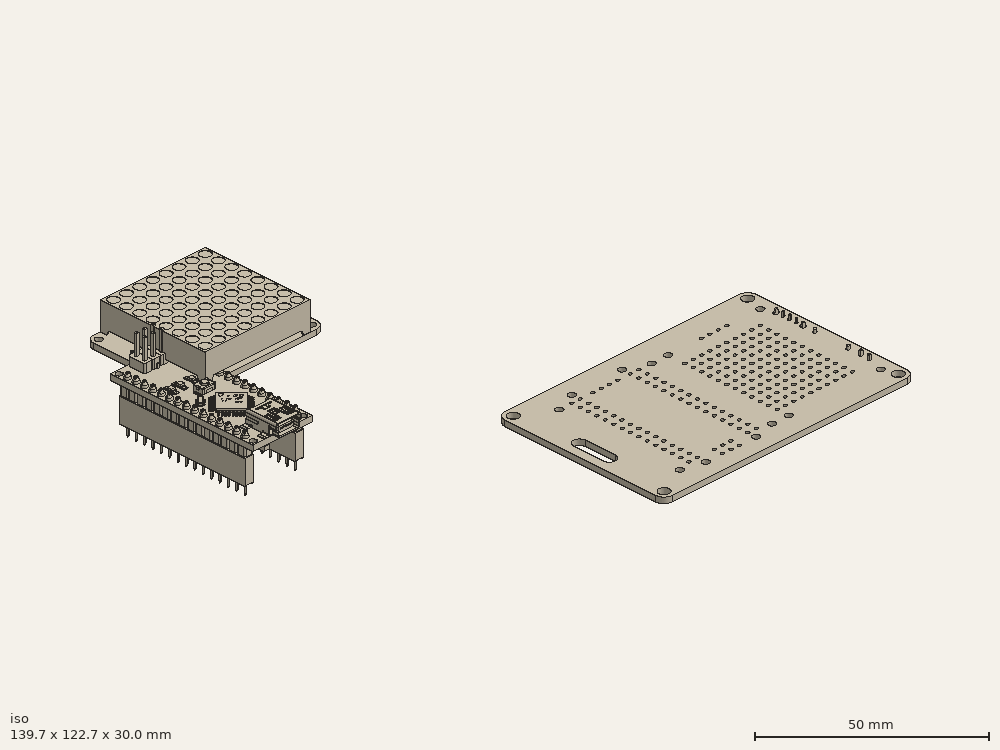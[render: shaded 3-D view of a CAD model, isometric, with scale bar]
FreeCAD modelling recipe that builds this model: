
FCSTD DOCUMENT  (FreeCAD 2022.709R28846 (Git))
Label: 8x8_badge
License: All rights reserved
LicenseURL: http://en.wikipedia.org/wiki/All_rights_reserved
objects: App::Link×150, Part::Feature×100, App::Part×8, PartDesign::CoordinateSystem×1, Sketcher::SketchObject×1
note: 102 computed .brp shape members not serialized (recipe doc carries the construction recipe); baked Part::Feature solids carry a one-line shape summary decoded from their .brp

FEATURE [PartDesign::CoordinateSystem] Local_CS_97b0
  AttacherType = Attacher::AttachEngine3D
  AttachmentSupport = -> [X_Axis001]
  MapMode = 2
  Support = -> [X_Axis001]
  TreeRank = 0
FEATURE [Part::Feature] Pcb_97b0
  TreeRank = 0
  shape: bbox 76.2 x 50.8 x 1.6 mm, 233 faces (baked)
FEATURE [Sketcher::SketchObject] PCB_Sketch_97b0
  ArcFitTolerance = 0
  FullyConstrained = false
  TreeRank = 0
  sketch-geometry (16):
    g0: LineSegment StartX=56.896 StartY=-85.852 StartZ=0 EndX=56.896 EndY=-76.708 EndZ=0
    g1: LineSegment StartX=53.34 StartY=-55.88 StartZ=0 EndX=124.46 EndY=-55.88 EndZ=0
    g2: LineSegment StartX=124.46 StartY=-106.68 StartZ=0 EndX=53.34 EndY=-106.68 EndZ=0
    g3: LineSegment StartX=127 StartY=-58.42 StartZ=0 EndX=127 EndY=-104.14 EndZ=0
    g4: LineSegment StartX=53.34 StartY=-76.708 StartZ=0 EndX=53.34 EndY=-85.852 EndZ=0
    g5: LineSegment StartX=50.8 StartY=-104.14 StartZ=0 EndX=50.8 EndY=-58.42 EndZ=0
    g6: ArcOfCircle CenterX=124.46 CenterY=-58.42 CenterZ=0 NormalX=0 NormalY=0 NormalZ=-1 AngleXU=1.5708 Radius=2.54 StartAngle=0 EndAngle=1.5708
    g7: ArcOfCircle CenterX=53.34 CenterY=-58.42 CenterZ=0 NormalX=0 NormalY=0 NormalZ=-1 AngleXU=3.01383e-07 Radius=2.54 StartAngle=0 EndAngle=1.5708
    g8: ArcOfCircle CenterX=55.118 CenterY=-85.852 CenterZ=0 NormalX=0 NormalY=0 NormalZ=-1 AngleXU=-3.14159 Radius=1.778 StartAngle=0 EndAngle=3.14159
    g9: ArcOfCircle CenterX=55.118 CenterY=-76.708 CenterZ=0 NormalX=0 NormalY=0 NormalZ=-1 AngleXU=8e-15 Radius=1.778 StartAngle=0 EndAngle=3.14159
    g10: ArcOfCircle CenterX=53.34 CenterY=-104.14 CenterZ=0 NormalX=0 NormalY=0 NormalZ=-1 AngleXU=-1.5708 Radius=2.54 StartAngle=0 EndAngle=1.5708
    g11: ArcOfCircle CenterX=124.46 CenterY=-104.14 CenterZ=0 NormalX=0 NormalY=0 NormalZ=-1 AngleXU=-3.14159 Radius=2.54 StartAngle=0 EndAngle=1.5708
    g12: Circle CenterX=124.46 CenterY=-58.42 CenterZ=0 NormalX=0 NormalY=0 NormalZ=1 AngleXU=0 Radius=1.524
    g13: Circle CenterX=53.34 CenterY=-104.14 CenterZ=0 NormalX=0 NormalY=0 NormalZ=1 AngleXU=0 Radius=1.524
    g14: Circle CenterX=124.46 CenterY=-104.14 CenterZ=0 NormalX=0 NormalY=0 NormalZ=1 AngleXU=0 Radius=1.524
    g15: Circle CenterX=53.34 CenterY=-58.42 CenterZ=0 NormalX=0 NormalY=0 NormalZ=1 AngleXU=0 Radius=1.524
  constraints (12):
    c: Coincident(g5,g10)
    c: Coincident(g5,g7)
    c: Coincident(g2,g10)
    c: Coincident(g4,g8)
    c: Coincident(g4,g9)
    c: Coincident(g1,g7)
    c: Coincident(g0,g8)
    c: Coincident(g0,g9)
    c: Coincident(g2,g11)
    c: Coincident(g1,g6)
    c: Coincident(g3,g11)
    c: Coincident(g3,g6)
FEATURE [Part::Feature] Shape  label="J135_PinHeader_1x01_P254mm_Vertical_da6c4aed0287"
  Placement = pos=(102.87,-71.12,0) rot=(0,0,1;1.5708rad)
  TreeRank = 0
  shape: bbox 2.54 x 2.54 x 11.54 mm, 28 faces (baked)
FEATURE [App::Link] J135_PinHeader_1x01_P254mm_Vertical_da6c4aed0287_ln_  label="J61_PinHeader_1x01_P254mm_Vertical_773ae547e81d"
  AutoLinkLabel = false
  AutoPlacement = true
  LinkPlacement = pos=(118.11,-91.44,0) rot=(0,0,1;1.5708rad)
  LinkedObject = -> Shape
  Placement = pos=(118.11,-91.44,0) rot=(0,0,1;1.5708rad)
  SyncGroupVisibility = false
  TreeRank = 0
  _LinkVersion = 1
FEATURE [App::Link] J135_PinHeader_1x01_P254mm_Vertical_da6c4aed0287_ln_001  label="J50_PinHeader_1x01_P254mm_Vertical_5aa259a9185c"
  AutoLinkLabel = false
  AutoPlacement = true
  LinkPlacement = pos=(115.57,-93.98,0) rot=(0,0,1;1.5708rad)
  LinkedObject = -> Shape
  Placement = pos=(115.57,-93.98,0) rot=(0,0,1;1.5708rad)
  SyncGroupVisibility = false
  TreeRank = 0
  _LinkVersion = 1
FEATURE [App::Link] J135_PinHeader_1x01_P254mm_Vertical_da6c4aed0287_ln_002  label="J2_PinHeader_1x01_P254mm_Vertical_c9b2285a6f13"
  AutoLinkLabel = false
  AutoPlacement = true
  LinkPlacement = pos=(66.04,-88.9,0) rot=(0,0,1;3.14159rad)
  LinkedObject = -> Shape
  Placement = pos=(66.04,-88.9,0) rot=(0,0,1;3.14159rad)
  SyncGroupVisibility = false
  TreeRank = 0
  _LinkVersion = 1
FEATURE [App::Link] J135_PinHeader_1x01_P254mm_Vertical_da6c4aed0287_ln_003  label="J140_PinHeader_1x01_P254mm_Vertical_72f53bb47756"
  AutoLinkLabel = false
  AutoPlacement = true
  LinkPlacement = pos=(115.57,-71.12,0) rot=(0,0,1;1.5708rad)
  LinkedObject = -> Shape
  Placement = pos=(115.57,-71.12,0) rot=(0,0,1;1.5708rad)
  SyncGroupVisibility = false
  TreeRank = 0
  _LinkVersion = 1
FEATURE [App::Link] J135_PinHeader_1x01_P254mm_Vertical_da6c4aed0287_ln_004  label="J124_PinHeader_1x01_P254mm_Vertical_2792789bb18d"
  AutoLinkLabel = false
  AutoPlacement = true
  LinkPlacement = pos=(100.33,-73.66,0) rot=(0,0,1;1.5708rad)
  LinkedObject = -> Shape
  Placement = pos=(100.33,-73.66,0) rot=(0,0,1;1.5708rad)
  SyncGroupVisibility = false
  TreeRank = 0
  _LinkVersion = 1
FEATURE [App::Link] J135_PinHeader_1x01_P254mm_Vertical_da6c4aed0287_ln_005  label="J17_PinHeader_1x01_P254mm_Vertical_b3db6972f96f"
  AutoLinkLabel = false
  AutoPlacement = true
  LinkPlacement = pos=(66.04,-99.06,0) rot=(0,0,1;3.14159rad)
  LinkedObject = -> Shape
  Placement = pos=(66.04,-99.06,0) rot=(0,0,1;3.14159rad)
  SyncGroupVisibility = false
  TreeRank = 0
  _LinkVersion = 1
FEATURE [App::Link] J135_PinHeader_1x01_P254mm_Vertical_da6c4aed0287_ln_006  label="J44_PinHeader_1x01_P254mm_Vertical_6a244c9ca252"
  AutoLinkLabel = false
  AutoPlacement = true
  LinkPlacement = pos=(100.33,-93.98,0) rot=(0,0,1;1.5708rad)
  LinkedObject = -> Shape
  Placement = pos=(100.33,-93.98,0) rot=(0,0,1;1.5708rad)
  SyncGroupVisibility = false
  TreeRank = 0
  _LinkVersion = 1
FEATURE [App::Link] J135_PinHeader_1x01_P254mm_Vertical_da6c4aed0287_ln_007  label="J69_PinHeader_1x01_P254mm_Vertical_9c543508d3f7"
  AutoLinkLabel = false
  AutoPlacement = true
  LinkPlacement = pos=(113.03,-88.9,0) rot=(0,0,1;1.5708rad)
  LinkedObject = -> Shape
  Placement = pos=(113.03,-88.9,0) rot=(0,0,1;1.5708rad)
  SyncGroupVisibility = false
  TreeRank = 0
  _LinkVersion = 1
FEATURE [App::Link] J135_PinHeader_1x01_P254mm_Vertical_da6c4aed0287_ln_008  label="J73_PinHeader_1x01_P254mm_Vertical_27754063a736"
  AutoLinkLabel = false
  AutoPlacement = true
  LinkPlacement = pos=(97.79,-86.36,0) rot=(0,0,1;1.5708rad)
  LinkedObject = -> Shape
  Placement = pos=(97.79,-86.36,0) rot=(0,0,1;1.5708rad)
  SyncGroupVisibility = false
  TreeRank = 0
  _LinkVersion = 1
FEATURE [App::Link] J135_PinHeader_1x01_P254mm_Vertical_da6c4aed0287_ln_009  label="J10_PinHeader_1x01_P254mm_Vertical_bf699268af4c"
  AutoLinkLabel = false
  AutoPlacement = true
  LinkPlacement = pos=(66.04,-68.58,0) rot=(0,0,1;3.14159rad)
  LinkedObject = -> Shape
  Placement = pos=(66.04,-68.58,0) rot=(0,0,1;3.14159rad)
  SyncGroupVisibility = false
  TreeRank = 0
  _LinkVersion = 1
FEATURE [App::Link] J135_PinHeader_1x01_P254mm_Vertical_da6c4aed0287_ln_010  label="J59_PinHeader_1x01_P254mm_Vertical_64cb25116942"
  AutoLinkLabel = false
  AutoPlacement = true
  LinkPlacement = pos=(113.03,-91.44,0) rot=(0,0,1;1.5708rad)
  LinkedObject = -> Shape
  Placement = pos=(113.03,-91.44,0) rot=(0,0,1;1.5708rad)
  SyncGroupVisibility = false
  TreeRank = 0
  _LinkVersion = 1
FEATURE [App::Link] J135_PinHeader_1x01_P254mm_Vertical_da6c4aed0287_ln_011  label="J41_PinHeader_1x01_P254mm_Vertical_46e97698a8e3"
  AutoLinkLabel = false
  AutoPlacement = true
  LinkPlacement = pos=(118.11,-96.52,0) rot=(0,0,1;1.5708rad)
  LinkedObject = -> Shape
  Placement = pos=(118.11,-96.52,0) rot=(0,0,1;1.5708rad)
  SyncGroupVisibility = false
  TreeRank = 0
  _LinkVersion = 1
FEATURE [App::Link] J135_PinHeader_1x01_P254mm_Vertical_da6c4aed0287_ln_012  label="J68_PinHeader_1x01_P254mm_Vertical_3277878d9fcc"
  AutoLinkLabel = false
  AutoPlacement = true
  LinkPlacement = pos=(110.49,-88.9,0) rot=(0,0,1;1.5708rad)
  LinkedObject = -> Shape
  Placement = pos=(110.49,-88.9,0) rot=(0,0,1;1.5708rad)
  SyncGroupVisibility = false
  TreeRank = 0
  _LinkVersion = 1
FEATURE [App::Link] J135_PinHeader_1x01_P254mm_Vertical_da6c4aed0287_ln_013  label="J106_PinHeader_1x01_P254mm_Vertical_6a619a310b17"
  AutoLinkLabel = false
  AutoPlacement = true
  LinkPlacement = pos=(105.41,-78.74,0) rot=(0,0,1;1.5708rad)
  LinkedObject = -> Shape
  Placement = pos=(105.41,-78.74,0) rot=(0,0,1;1.5708rad)
  SyncGroupVisibility = false
  TreeRank = 0
  _LinkVersion = 1
FEATURE [App::Link] J135_PinHeader_1x01_P254mm_Vertical_da6c4aed0287_ln_014  label="J27_PinHeader_1x01_P254mm_Vertical_58b75af8ef85"
  AutoLinkLabel = false
  AutoPlacement = true
  LinkPlacement = pos=(86.36,-99.06,0) rot=(0,0,1;3.14159rad)
  LinkedObject = -> Shape
  Placement = pos=(86.36,-99.06,0) rot=(0,0,1;3.14159rad)
  SyncGroupVisibility = false
  TreeRank = 0
  _LinkVersion = 1
FEATURE [App::Link] J135_PinHeader_1x01_P254mm_Vertical_da6c4aed0287_ln_015  label="J95_PinHeader_1x01_P254mm_Vertical_eca1b71ce0e1"
  AutoLinkLabel = false
  AutoPlacement = true
  LinkPlacement = pos=(102.87,-81.28,0) rot=(0,0,1;1.5708rad)
  LinkedObject = -> Shape
  Placement = pos=(102.87,-81.28,0) rot=(0,0,1;1.5708rad)
  SyncGroupVisibility = false
  TreeRank = 0
  _LinkVersion = 1
FEATURE [App::Link] J135_PinHeader_1x01_P254mm_Vertical_da6c4aed0287_ln_016  label="J24_PinHeader_1x01_P254mm_Vertical_b4f680f1af2d"
  AutoLinkLabel = false
  AutoPlacement = true
  LinkPlacement = pos=(86.36,-73.66,0) rot=(0,0,1;3.14159rad)
  LinkedObject = -> Shape
  Placement = pos=(86.36,-73.66,0) rot=(0,0,1;3.14159rad)
  SyncGroupVisibility = false
  TreeRank = 0
  _LinkVersion = 1
FEATURE [App::Link] J135_PinHeader_1x01_P254mm_Vertical_da6c4aed0287_ln_017  label="J16_PinHeader_1x01_P254mm_Vertical_e98a18c1f6ef"
  AutoLinkLabel = false
  AutoPlacement = true
  LinkPlacement = pos=(66.04,-96.52,0) rot=(0,0,1;3.14159rad)
  LinkedObject = -> Shape
  Placement = pos=(66.04,-96.52,0) rot=(0,0,1;3.14159rad)
  SyncGroupVisibility = false
  TreeRank = 0
  _LinkVersion = 1
FEATURE [App::Link] J135_PinHeader_1x01_P254mm_Vertical_da6c4aed0287_ln_018  label="J77_PinHeader_1x01_P254mm_Vertical_00ab3d87ffcd"
  AutoLinkLabel = false
  AutoPlacement = true
  LinkPlacement = pos=(107.95,-86.36,0) rot=(0,0,1;1.5708rad)
  LinkedObject = -> Shape
  Placement = pos=(107.95,-86.36,0) rot=(0,0,1;1.5708rad)
  SyncGroupVisibility = false
  TreeRank = 0
  _LinkVersion = 1
FEATURE [App::Link] J135_PinHeader_1x01_P254mm_Vertical_da6c4aed0287_ln_019  label="J109_PinHeader_1x01_P254mm_Vertical_e80f5348a3fd"
  AutoLinkLabel = false
  AutoPlacement = true
  LinkPlacement = pos=(113.03,-78.74,0) rot=(0,0,1;1.5708rad)
  LinkedObject = -> Shape
  Placement = pos=(113.03,-78.74,0) rot=(0,0,1;1.5708rad)
  SyncGroupVisibility = false
  TreeRank = 0
  _LinkVersion = 1
FEATURE [App::Link] J135_PinHeader_1x01_P254mm_Vertical_da6c4aed0287_ln_020  label="J139_PinHeader_1x01_P254mm_Vertical_62e98df2bb86"
  AutoLinkLabel = false
  AutoPlacement = true
  LinkPlacement = pos=(113.03,-71.12,0) rot=(0,0,1;1.5708rad)
  LinkedObject = -> Shape
  Placement = pos=(113.03,-71.12,0) rot=(0,0,1;1.5708rad)
  SyncGroupVisibility = false
  TreeRank = 0
  _LinkVersion = 1
FEATURE [App::Link] J135_PinHeader_1x01_P254mm_Vertical_da6c4aed0287_ln_021  label="J123_PinHeader_1x01_P254mm_Vertical_de5b5ec60197"
  AutoLinkLabel = false
  AutoPlacement = true
  LinkPlacement = pos=(97.79,-73.66,0) rot=(0,0,1;1.5708rad)
  LinkedObject = -> Shape
  Placement = pos=(97.79,-73.66,0) rot=(0,0,1;1.5708rad)
  SyncGroupVisibility = false
  TreeRank = 0
  _LinkVersion = 1
FEATURE [App::Link] J135_PinHeader_1x01_P254mm_Vertical_da6c4aed0287_ln_022  label="J5_PinHeader_1x01_P254mm_Vertical_cd3758c55ec9"
  AutoLinkLabel = false
  AutoPlacement = true
  LinkPlacement = pos=(66.04,-81.28,0) rot=(0,0,1;3.14159rad)
  LinkedObject = -> Shape
  Placement = pos=(66.04,-81.28,0) rot=(0,0,1;3.14159rad)
  SyncGroupVisibility = false
  TreeRank = 0
  _LinkVersion = 1
FEATURE [App::Link] J135_PinHeader_1x01_P254mm_Vertical_da6c4aed0287_ln_023  label="J98_PinHeader_1x01_P254mm_Vertical_84919f920f7b"
  AutoLinkLabel = false
  AutoPlacement = true
  LinkPlacement = pos=(110.49,-81.28,0) rot=(0,0,1;1.5708rad)
  LinkedObject = -> Shape
  Placement = pos=(110.49,-81.28,0) rot=(0,0,1;1.5708rad)
  SyncGroupVisibility = false
  TreeRank = 0
  _LinkVersion = 1
FEATURE [App::Link] J135_PinHeader_1x01_P254mm_Vertical_da6c4aed0287_ln_024  label="J85_PinHeader_1x01_P254mm_Vertical_de25c8d6ebfc"
  AutoLinkLabel = false
  AutoPlacement = true
  LinkPlacement = pos=(102.87,-83.82,0) rot=(0,0,1;1.5708rad)
  LinkedObject = -> Shape
  Placement = pos=(102.87,-83.82,0) rot=(0,0,1;1.5708rad)
  SyncGroupVisibility = false
  TreeRank = 0
  _LinkVersion = 1
FEATURE [App::Link] J135_PinHeader_1x01_P254mm_Vertical_da6c4aed0287_ln_025  label="J78_PinHeader_1x01_P254mm_Vertical_6cd363f12a80"
  AutoLinkLabel = false
  AutoPlacement = true
  LinkPlacement = pos=(110.49,-86.36,0) rot=(0,0,1;1.5708rad)
  LinkedObject = -> Shape
  Placement = pos=(110.49,-86.36,0) rot=(0,0,1;1.5708rad)
  SyncGroupVisibility = false
  TreeRank = 0
  _LinkVersion = 1
FEATURE [App::Link] J135_PinHeader_1x01_P254mm_Vertical_da6c4aed0287_ln_026  label="J92_PinHeader_1x01_P254mm_Vertical_7b98299fb2b6"
  AutoLinkLabel = false
  AutoPlacement = true
  LinkPlacement = pos=(95.25,-81.28,0) rot=(0,0,1;1.5708rad)
  LinkedObject = -> Shape
  Placement = pos=(95.25,-81.28,0) rot=(0,0,1;1.5708rad)
  SyncGroupVisibility = false
  TreeRank = 0
  _LinkVersion = 1
FEATURE [App::Link] J135_PinHeader_1x01_P254mm_Vertical_da6c4aed0287_ln_027  label="J146_PinHeader_1x01_P254mm_Vertical_d33f2c13bd96"
  AutoLinkLabel = false
  AutoPlacement = true
  LinkPlacement = pos=(105.41,-68.58,0) rot=(0,0,1;1.5708rad)
  LinkedObject = -> Shape
  Placement = pos=(105.41,-68.58,0) rot=(0,0,1;1.5708rad)
  SyncGroupVisibility = false
  TreeRank = 0
  _LinkVersion = 1
FEATURE [App::Link] J135_PinHeader_1x01_P254mm_Vertical_da6c4aed0287_ln_028  label="J12_PinHeader_1x01_P254mm_Vertical_9e959caa93af"
  AutoLinkLabel = false
  AutoPlacement = true
  LinkPlacement = pos=(66.04,-63.5,0) rot=(0,0,1;3.14159rad)
  LinkedObject = -> Shape
  Placement = pos=(66.04,-63.5,0) rot=(0,0,1;3.14159rad)
  SyncGroupVisibility = false
  TreeRank = 0
  _LinkVersion = 1
FEATURE [App::Link] J135_PinHeader_1x01_P254mm_Vertical_da6c4aed0287_ln_029  label="J74_PinHeader_1x01_P254mm_Vertical_ebb3536fd29e"
  AutoLinkLabel = false
  AutoPlacement = true
  LinkPlacement = pos=(100.33,-86.36,0) rot=(0,0,1;1.5708rad)
  LinkedObject = -> Shape
  Placement = pos=(100.33,-86.36,0) rot=(0,0,1;1.5708rad)
  SyncGroupVisibility = false
  TreeRank = 0
  _LinkVersion = 1
FEATURE [App::Link] J135_PinHeader_1x01_P254mm_Vertical_da6c4aed0287_ln_030  label="J58_PinHeader_1x01_P254mm_Vertical_9a14729430aa"
  AutoLinkLabel = false
  AutoPlacement = true
  LinkPlacement = pos=(110.49,-91.44,0) rot=(0,0,1;1.5708rad)
  LinkedObject = -> Shape
  Placement = pos=(110.49,-91.44,0) rot=(0,0,1;1.5708rad)
  SyncGroupVisibility = false
  TreeRank = 0
  _LinkVersion = 1
FEATURE [App::Link] J135_PinHeader_1x01_P254mm_Vertical_da6c4aed0287_ln_031  label="J130_PinHeader_1x01_P254mm_Vertical_e60d4ac48af7"
  AutoLinkLabel = false
  AutoPlacement = true
  LinkPlacement = pos=(115.57,-73.66,0) rot=(0,0,1;1.5708rad)
  LinkedObject = -> Shape
  Placement = pos=(115.57,-73.66,0) rot=(0,0,1;1.5708rad)
  SyncGroupVisibility = false
  TreeRank = 0
  _LinkVersion = 1
FEATURE [App::Link] J135_PinHeader_1x01_P254mm_Vertical_da6c4aed0287_ln_032  label="J99_PinHeader_1x01_P254mm_Vertical_5f2264147a32"
  AutoLinkLabel = false
  AutoPlacement = true
  LinkPlacement = pos=(113.03,-81.28,0) rot=(0,0,1;1.5708rad)
  LinkedObject = -> Shape
  Placement = pos=(113.03,-81.28,0) rot=(0,0,1;1.5708rad)
  SyncGroupVisibility = false
  TreeRank = 0
  _LinkVersion = 1
FEATURE [App::Link] J135_PinHeader_1x01_P254mm_Vertical_da6c4aed0287_ln_033  label="J107_PinHeader_1x01_P254mm_Vertical_2f2c6f5fa7e0"
  AutoLinkLabel = false
  AutoPlacement = true
  LinkPlacement = pos=(107.95,-78.74,0) rot=(0,0,1;1.5708rad)
  LinkedObject = -> Shape
  Placement = pos=(107.95,-78.74,0) rot=(0,0,1;1.5708rad)
  SyncGroupVisibility = false
  TreeRank = 0
  _LinkVersion = 1
FEATURE [App::Link] J135_PinHeader_1x01_P254mm_Vertical_da6c4aed0287_ln_034  label="J117_PinHeader_1x01_P254mm_Vertical_64dd41409d9f"
  AutoLinkLabel = false
  AutoPlacement = true
  LinkPlacement = pos=(107.95,-76.2,0) rot=(0,0,1;1.5708rad)
  LinkedObject = -> Shape
  Placement = pos=(107.95,-76.2,0) rot=(0,0,1;1.5708rad)
  SyncGroupVisibility = false
  TreeRank = 0
  _LinkVersion = 1
FEATURE [App::Link] J135_PinHeader_1x01_P254mm_Vertical_da6c4aed0287_ln_035  label="J60_PinHeader_1x01_P254mm_Vertical_14a406c96dca"
  AutoLinkLabel = false
  AutoPlacement = true
  LinkPlacement = pos=(115.57,-91.44,0) rot=(0,0,1;1.5708rad)
  LinkedObject = -> Shape
  Placement = pos=(115.57,-91.44,0) rot=(0,0,1;1.5708rad)
  SyncGroupVisibility = false
  TreeRank = 0
  _LinkVersion = 1
FEATURE [App::Link] J135_PinHeader_1x01_P254mm_Vertical_da6c4aed0287_ln_036  label="J144_PinHeader_1x01_P254mm_Vertical_684e6d7036d3"
  AutoLinkLabel = false
  AutoPlacement = true
  LinkPlacement = pos=(100.33,-68.58,0) rot=(0,0,1;1.5708rad)
  LinkedObject = -> Shape
  Placement = pos=(100.33,-68.58,0) rot=(0,0,1;1.5708rad)
  SyncGroupVisibility = false
  TreeRank = 0
  _LinkVersion = 1
FEATURE [App::Link] J135_PinHeader_1x01_P254mm_Vertical_da6c4aed0287_ln_037  label="J3_PinHeader_1x01_P254mm_Vertical_85c80b18d1db"
  AutoLinkLabel = false
  AutoPlacement = true
  LinkPlacement = pos=(66.04,-86.36,0) rot=(0,0,1;3.14159rad)
  LinkedObject = -> Shape
  Placement = pos=(66.04,-86.36,0) rot=(0,0,1;3.14159rad)
  SyncGroupVisibility = false
  TreeRank = 0
  _LinkVersion = 1
FEATURE [App::Link] J135_PinHeader_1x01_P254mm_Vertical_da6c4aed0287_ln_038  label="J113_PinHeader_1x01_P254mm_Vertical_3395830e7b0b"
  AutoLinkLabel = false
  AutoPlacement = true
  LinkPlacement = pos=(97.79,-76.2,0) rot=(0,0,1;1.5708rad)
  LinkedObject = -> Shape
  Placement = pos=(97.79,-76.2,0) rot=(0,0,1;1.5708rad)
  SyncGroupVisibility = false
  TreeRank = 0
  _LinkVersion = 1
FEATURE [App::Link] J135_PinHeader_1x01_P254mm_Vertical_da6c4aed0287_ln_039  label="J90_PinHeader_1x01_P254mm_Vertical_ad3d40650960"
  AutoLinkLabel = false
  AutoPlacement = true
  LinkPlacement = pos=(115.57,-83.82,0) rot=(0,0,1;1.5708rad)
  LinkedObject = -> Shape
  Placement = pos=(115.57,-83.82,0) rot=(0,0,1;1.5708rad)
  SyncGroupVisibility = false
  TreeRank = 0
  _LinkVersion = 1
FEATURE [App::Link] J135_PinHeader_1x01_P254mm_Vertical_da6c4aed0287_ln_040  label="J36_PinHeader_1x01_P254mm_Vertical_8b62ba1c48d5"
  AutoLinkLabel = false
  AutoPlacement = true
  LinkPlacement = pos=(105.41,-96.52,0) rot=(0,0,1;1.5708rad)
  LinkedObject = -> Shape
  Placement = pos=(105.41,-96.52,0) rot=(0,0,1;1.5708rad)
  SyncGroupVisibility = false
  TreeRank = 0
  _LinkVersion = 1
FEATURE [App::Link] J135_PinHeader_1x01_P254mm_Vertical_da6c4aed0287_ln_041  label="J129_PinHeader_1x01_P254mm_Vertical_d9d08025a7fb"
  AutoLinkLabel = false
  AutoPlacement = true
  LinkPlacement = pos=(113.03,-73.66,0) rot=(0,0,1;1.5708rad)
  LinkedObject = -> Shape
  Placement = pos=(113.03,-73.66,0) rot=(0,0,1;1.5708rad)
  SyncGroupVisibility = false
  TreeRank = 0
  _LinkVersion = 1
FEATURE [App::Link] J135_PinHeader_1x01_P254mm_Vertical_da6c4aed0287_ln_042  label="J127_PinHeader_1x01_P254mm_Vertical_3bb2cf8e585d"
  AutoLinkLabel = false
  AutoPlacement = true
  LinkPlacement = pos=(107.95,-73.66,0) rot=(0,0,1;1.5708rad)
  LinkedObject = -> Shape
  Placement = pos=(107.95,-73.66,0) rot=(0,0,1;1.5708rad)
  SyncGroupVisibility = false
  TreeRank = 0
  _LinkVersion = 1
FEATURE [App::Link] J135_PinHeader_1x01_P254mm_Vertical_da6c4aed0287_ln_043  label="J136_PinHeader_1x01_P254mm_Vertical_428c39a7f71f"
  AutoLinkLabel = false
  AutoPlacement = true
  LinkPlacement = pos=(105.41,-71.12,0) rot=(0,0,1;1.5708rad)
  LinkedObject = -> Shape
  Placement = pos=(105.41,-71.12,0) rot=(0,0,1;1.5708rad)
  SyncGroupVisibility = false
  TreeRank = 0
  _LinkVersion = 1
FEATURE [App::Link] J135_PinHeader_1x01_P254mm_Vertical_da6c4aed0287_ln_044  label="J14_PinHeader_1x01_P254mm_Vertical_bf06523fea07"
  AutoLinkLabel = false
  AutoPlacement = true
  LinkPlacement = pos=(66.04,-93.98,0) rot=(0,0,1;3.14159rad)
  LinkedObject = -> Shape
  Placement = pos=(66.04,-93.98,0) rot=(0,0,1;3.14159rad)
  SyncGroupVisibility = false
  TreeRank = 0
  _LinkVersion = 1
FEATURE [App::Link] J135_PinHeader_1x01_P254mm_Vertical_da6c4aed0287_ln_045  label="J147_PinHeader_1x01_P254mm_Vertical_30fb8c6109c9"
  AutoLinkLabel = false
  AutoPlacement = true
  LinkPlacement = pos=(107.95,-68.58,0) rot=(0,0,1;1.5708rad)
  LinkedObject = -> Shape
  Placement = pos=(107.95,-68.58,0) rot=(0,0,1;1.5708rad)
  SyncGroupVisibility = false
  TreeRank = 0
  _LinkVersion = 1
FEATURE [App::Link] J135_PinHeader_1x01_P254mm_Vertical_da6c4aed0287_ln_046  label="J31_PinHeader_1x01_P254mm_Vertical_ee7d523646c7"
  AutoLinkLabel = false
  AutoPlacement = true
  LinkPlacement = pos=(66.04,-91.44,0) rot=(0,0,1;3.14159rad)
  LinkedObject = -> Shape
  Placement = pos=(66.04,-91.44,0) rot=(0,0,1;3.14159rad)
  SyncGroupVisibility = false
  TreeRank = 0
  _LinkVersion = 1
FEATURE [App::Link] J135_PinHeader_1x01_P254mm_Vertical_da6c4aed0287_ln_047  label="J87_PinHeader_1x01_P254mm_Vertical_cbb93bdeda80"
  AutoLinkLabel = false
  AutoPlacement = true
  LinkPlacement = pos=(107.95,-83.82,0) rot=(0,0,1;1.5708rad)
  LinkedObject = -> Shape
  Placement = pos=(107.95,-83.82,0) rot=(0,0,1;1.5708rad)
  SyncGroupVisibility = false
  TreeRank = 0
  _LinkVersion = 1
FEATURE [App::Link] J135_PinHeader_1x01_P254mm_Vertical_da6c4aed0287_ln_048  label="J66_PinHeader_1x01_P254mm_Vertical_c71becf67217"
  AutoLinkLabel = false
  AutoPlacement = true
  LinkPlacement = pos=(105.41,-88.9,0) rot=(0,0,1;1.5708rad)
  LinkedObject = -> Shape
  Placement = pos=(105.41,-88.9,0) rot=(0,0,1;1.5708rad)
  SyncGroupVisibility = false
  TreeRank = 0
  _LinkVersion = 1
FEATURE [App::Link] J135_PinHeader_1x01_P254mm_Vertical_da6c4aed0287_ln_049  label="J148_PinHeader_1x01_P254mm_Vertical_3caf071db488"
  AutoLinkLabel = false
  AutoPlacement = true
  LinkPlacement = pos=(110.49,-68.58,0) rot=(0,0,1;1.5708rad)
  LinkedObject = -> Shape
  Placement = pos=(110.49,-68.58,0) rot=(0,0,1;1.5708rad)
  SyncGroupVisibility = false
  TreeRank = 0
  _LinkVersion = 1
FEATURE [App::Link] J135_PinHeader_1x01_P254mm_Vertical_da6c4aed0287_ln_050  label="J116_PinHeader_1x01_P254mm_Vertical_249d3775cc33"
  AutoLinkLabel = false
  AutoPlacement = true
  LinkPlacement = pos=(105.41,-76.2,0) rot=(0,0,1;1.5708rad)
  LinkedObject = -> Shape
  Placement = pos=(105.41,-76.2,0) rot=(0,0,1;1.5708rad)
  SyncGroupVisibility = false
  TreeRank = 0
  _LinkVersion = 1
FEATURE [App::Link] J135_PinHeader_1x01_P254mm_Vertical_da6c4aed0287_ln_051  label="J122_PinHeader_1x01_P254mm_Vertical_a719b4abe7b1"
  AutoLinkLabel = false
  AutoPlacement = true
  LinkPlacement = pos=(95.25,-73.66,0) rot=(0,0,1;1.5708rad)
  LinkedObject = -> Shape
  Placement = pos=(95.25,-73.66,0) rot=(0,0,1;1.5708rad)
  SyncGroupVisibility = false
  TreeRank = 0
  _LinkVersion = 1
FEATURE [App::Link] J135_PinHeader_1x01_P254mm_Vertical_da6c4aed0287_ln_052  label="J119_PinHeader_1x01_P254mm_Vertical_f1aa55f767d0"
  AutoLinkLabel = false
  AutoPlacement = true
  LinkPlacement = pos=(113.03,-76.2,0) rot=(0,0,1;1.5708rad)
  LinkedObject = -> Shape
  Placement = pos=(113.03,-76.2,0) rot=(0,0,1;1.5708rad)
  SyncGroupVisibility = false
  TreeRank = 0
  _LinkVersion = 1
FEATURE [App::Link] J135_PinHeader_1x01_P254mm_Vertical_da6c4aed0287_ln_053  label="J133_PinHeader_1x01_P254mm_Vertical_cecdf641149b"
  AutoLinkLabel = false
  AutoPlacement = true
  LinkPlacement = pos=(97.79,-71.12,0) rot=(0,0,1;1.5708rad)
  LinkedObject = -> Shape
  Placement = pos=(97.79,-71.12,0) rot=(0,0,1;1.5708rad)
  SyncGroupVisibility = false
  TreeRank = 0
  _LinkVersion = 1
FEATURE [App::Link] J135_PinHeader_1x01_P254mm_Vertical_da6c4aed0287_ln_054  label="J142_PinHeader_1x01_P254mm_Vertical_d780b6723fc1"
  AutoLinkLabel = false
  AutoPlacement = true
  LinkPlacement = pos=(95.25,-68.58,0) rot=(0,0,1;1.5708rad)
  LinkedObject = -> Shape
  Placement = pos=(95.25,-68.58,0) rot=(0,0,1;1.5708rad)
  SyncGroupVisibility = false
  TreeRank = 0
  _LinkVersion = 1
FEATURE [App::Link] J135_PinHeader_1x01_P254mm_Vertical_da6c4aed0287_ln_055  label="J118_PinHeader_1x01_P254mm_Vertical_971ca6a70be6"
  AutoLinkLabel = false
  AutoPlacement = true
  LinkPlacement = pos=(110.49,-76.2,0) rot=(0,0,1;1.5708rad)
  LinkedObject = -> Shape
  Placement = pos=(110.49,-76.2,0) rot=(0,0,1;1.5708rad)
  SyncGroupVisibility = false
  TreeRank = 0
  _LinkVersion = 1
FEATURE [App::Link] J135_PinHeader_1x01_P254mm_Vertical_da6c4aed0287_ln_056  label="J28_PinHeader_1x01_P254mm_Vertical_d89022d6458d"
  AutoLinkLabel = false
  AutoPlacement = true
  LinkPlacement = pos=(86.36,-91.44,0) rot=(0,0,1;3.14159rad)
  LinkedObject = -> Shape
  Placement = pos=(86.36,-91.44,0) rot=(0,0,1;3.14159rad)
  SyncGroupVisibility = false
  TreeRank = 0
  _LinkVersion = 1
FEATURE [Part::Feature] Part__Feature  label="Adafruit_1_2inch_8x8_backpack_v2_cp001_sp"
  TreeRank = 0
  shape: bbox 40.64 x 32 x 1.57 mm, 45 faces (baked)
FEATURE [Part::Feature] Part__Feature001  label="Adafruit_1_2inch_8x8_backpack_v2_cp001_sp001"
  TreeRank = 0
  shape: bbox 31.8 x 31.8 x 11.5 mm, 186 faces (baked)
FEATURE [Part::Feature] Part__Feature002  label="Adafruit_1_2inch_8x8_backpack_v2_cp001_sp002"
  TreeRank = 0
  shape: bbox 1.19 x 1.94 x 0.79 mm, 6 faces (baked)
FEATURE [Part::Feature] Part__Feature003  label="Adafruit_1_2inch_8x8_backpack_v2_cp001_sp003"
  TreeRank = 0
  shape: bbox 1.25 x 0.5 x 0.85 mm, 30 faces (baked)
FEATURE [Part::Feature] Part__Feature004  label="Adafruit_1_2inch_8x8_backpack_v2_cp001_sp004"
  TreeRank = 0
  shape: bbox 1.25 x 0.5 x 0.85 mm, 30 faces (baked)
FEATURE [Part::Feature] Part__Feature005  label="Adafruit_1_2inch_8x8_backpack_v2_cp001_sp005"
  TreeRank = 0
  shape: bbox 1.19 x 1.94 x 0.79 mm, 6 faces (baked)
FEATURE [Part::Feature] Part__Feature006  label="Adafruit_1_2inch_8x8_backpack_v2_cp001_sp006"
  TreeRank = 0
  shape: bbox 1.25 x 0.5 x 0.85 mm, 30 faces (baked)
FEATURE [Part::Feature] Part__Feature007  label="Adafruit_1_2inch_8x8_backpack_v2_cp001_sp007"
  TreeRank = 0
  shape: bbox 1.25 x 0.5 x 0.85 mm, 30 faces (baked)
FEATURE [Part::Feature] Part__Feature008  label="Adafruit_1_2inch_8x8_backpack_v2_cp001_sp008"
  TreeRank = 0
  shape: bbox 1.19 x 1.94 x 0.79 mm, 6 faces (baked)
FEATURE [Part::Feature] Part__Feature009  label="Adafruit_1_2inch_8x8_backpack_v2_cp001_sp009"
  TreeRank = 0
  shape: bbox 1.25 x 0.5 x 0.85 mm, 30 faces (baked)
FEATURE [Part::Feature] Part__Feature010  label="Adafruit_1_2inch_8x8_backpack_v2_cp001_sp010"
  TreeRank = 0
  shape: bbox 1.25 x 0.5 x 0.85 mm, 30 faces (baked)
FEATURE [Part::Feature] Part__Feature011  label="Adafruit_1_2inch_8x8_backpack_v2_cp001_sp011"
  TreeRank = 0
  shape: bbox 1.19 x 1.94 x 0.79 mm, 6 faces (baked)
FEATURE [Part::Feature] Part__Feature012  label="Adafruit_1_2inch_8x8_backpack_v2_cp001_sp012"
  TreeRank = 0
  shape: bbox 1.25 x 0.5 x 0.85 mm, 30 faces (baked)
FEATURE [Part::Feature] Part__Feature013  label="Adafruit_1_2inch_8x8_backpack_v2_cp001_sp013"
  TreeRank = 0
  shape: bbox 1.25 x 0.5 x 0.85 mm, 30 faces (baked)
FEATURE [Part::Feature] Part__Feature014  label="Adafruit_1_2inch_8x8_backpack_v2_cp001_sp014"
  TreeRank = 0
  shape: bbox 1.19 x 1.94 x 0.79 mm, 6 faces (baked)
FEATURE [Part::Feature] Part__Feature015  label="Adafruit_1_2inch_8x8_backpack_v2_cp001_sp015"
  TreeRank = 0
  shape: bbox 1.25 x 0.5 x 0.85 mm, 30 faces (baked)
FEATURE [Part::Feature] Part__Feature016  label="Adafruit_1_2inch_8x8_backpack_v2_cp001_sp016"
  TreeRank = 0
  shape: bbox 1.25 x 0.5 x 0.85 mm, 30 faces (baked)
FEATURE [Part::Feature] Part__Feature017  label="Adafruit_1_2inch_8x8_backpack_v2_cp001_sp017"
  TreeRank = 0
  shape: bbox 1.35 x 2.7 x 1.1 mm, 38 faces (baked)
FEATURE [Part::Feature] Part__Feature018  label="Adafruit_1_2inch_8x8_backpack_v2_cp001_sp018"
  TreeRank = 0
  shape: bbox 1.25 x 2 x 1 mm, 14 faces (baked)
FEATURE [Part::Feature] Part__Feature019  label="Adafruit_1_2inch_8x8_backpack_v2_cp001_sp019"
  TreeRank = 0
  shape: bbox 18 x 10 x 2.65 mm, 376 faces (baked)
FEATURE [Part::Feature] Part__Feature020  label="Adafruit_1_2inch_8x8_backpack_v2_cp001_sp020"
  TreeRank = 0
  shape: bbox 2.54 x 10.16 x 11.54 mm, 100 faces (baked)
FEATURE [Part::Feature] Part__Feature021  label="Adafruit_1_2inch_8x8_backpack_v2_cp001_sp021"
  TreeRank = 0
  shape: bbox 2.54 x 10.16 x 10.1 mm, 134 faces (baked)
FEATURE [App::Part] Adafruit_1_2inch_8x8_backpack_v2_cp001_sp  label="J1_Adafruit_1_2inch_8x8_backpack_v2_cp001_sp022_606130f15359"
  ClaimAllChildren = false
  ExportMode = 1
  Group = -> [Part__Feature,Part__Feature001,Part__Feature002,Part__Feature003,Part__Feature004,Part__Feature005,Part__Feature006,Part__Feature007,Part__Feature008,Part__Feature009,Part__Feature010,Part__Feature011,Part__Feature012,Part__Feature013,Part__Feature014,Part__Feature015,Part__Feature016,Part__Feature017,Part__Feature018,Part__Feature019,Part__Feature020,Part__Feature021]
  Origin = -> Origin008
  Placement = pos=(109.22,-63.5,0) rot=(0,0,-1;1.5708rad)
  TreeRank = 0
  _ExportChildren = -> [Part__Feature,Part__Feature001,Part__Feature002,Part__Feature003,Part__Feature004,Part__Feature005,Part__Feature006,Part__Feature007,Part__Feature008,Part__Feature009,Part__Feature010,Part__Feature011,Part__Feature012,Part__Feature013,Part__Feature014,Part__Feature015,Part__Feature016,Part__Feature017,Part__Feature018,Part__Feature019,Part__Feature020,Part__Feature021]
  _GroupVersion = 1
FEATURE [App::Link] J135_PinHeader_1x01_P254mm_Vertical_da6c4aed0287_ln_057  label="J13_PinHeader_1x01_P254mm_Vertical_f9c51dc1377b"
  AutoLinkLabel = false
  AutoPlacement = true
  LinkPlacement = pos=(86.36,-63.5,0) rot=(0,0,1;3.14159rad)
  LinkedObject = -> Shape
  Placement = pos=(86.36,-63.5,0) rot=(0,0,1;3.14159rad)
  SyncGroupVisibility = false
  TreeRank = 0
  _LinkVersion = 1
FEATURE [App::Link] J1_Adafruit_1_2inch_8x8_backpack_v2_cp001_sp022_606130f15359_ln_  label="LED1_Adafruit_1_2inch_8x8_backpack_v2_cp001_sp022_4a1c2dfe1e64"
  AutoLinkLabel = false
  AutoPlacement = true
  LinkPlacement = pos=(76.2,-63.5,0) rot=(0,0,-1;1.5708rad)
  LinkedObject = -> Adafruit_1_2inch_8x8_backpack_v2_cp001_sp
  Placement = pos=(76.2,-63.5,0) rot=(0,0,-1;1.5708rad)
  SyncGroupVisibility = false
  TreeRank = 0
  _LinkVersion = 1
FEATURE [App::Link] J135_PinHeader_1x01_P254mm_Vertical_da6c4aed0287_ln_058  label="J45_PinHeader_1x01_P254mm_Vertical_037e9dbc6d28"
  AutoLinkLabel = false
  AutoPlacement = true
  LinkPlacement = pos=(102.87,-93.98,0) rot=(0,0,1;1.5708rad)
  LinkedObject = -> Shape
  Placement = pos=(102.87,-93.98,0) rot=(0,0,1;1.5708rad)
  SyncGroupVisibility = false
  TreeRank = 0
  _LinkVersion = 1
FEATURE [App::Link] J135_PinHeader_1x01_P254mm_Vertical_da6c4aed0287_ln_059  label="J88_PinHeader_1x01_P254mm_Vertical_f91dea8db7ee"
  AutoLinkLabel = false
  AutoPlacement = true
  LinkPlacement = pos=(110.49,-83.82,0) rot=(0,0,1;1.5708rad)
  LinkedObject = -> Shape
  Placement = pos=(110.49,-83.82,0) rot=(0,0,1;1.5708rad)
  SyncGroupVisibility = false
  TreeRank = 0
  _LinkVersion = 1
FEATURE [App::Link] J135_PinHeader_1x01_P254mm_Vertical_da6c4aed0287_ln_060  label="J125_PinHeader_1x01_P254mm_Vertical_db89102eea80"
  AutoLinkLabel = false
  AutoPlacement = true
  LinkPlacement = pos=(102.87,-73.66,0) rot=(0,0,1;1.5708rad)
  LinkedObject = -> Shape
  Placement = pos=(102.87,-73.66,0) rot=(0,0,1;1.5708rad)
  SyncGroupVisibility = false
  TreeRank = 0
  _LinkVersion = 1
FEATURE [App::Link] J135_PinHeader_1x01_P254mm_Vertical_da6c4aed0287_ln_061  label="J57_PinHeader_1x01_P254mm_Vertical_bb6de2ac7262"
  AutoLinkLabel = false
  AutoPlacement = true
  LinkPlacement = pos=(107.95,-91.44,0) rot=(0,0,1;1.5708rad)
  LinkedObject = -> Shape
  Placement = pos=(107.95,-91.44,0) rot=(0,0,1;1.5708rad)
  SyncGroupVisibility = false
  TreeRank = 0
  _LinkVersion = 1
FEATURE [App::Link] J135_PinHeader_1x01_P254mm_Vertical_da6c4aed0287_ln_062  label="J18_PinHeader_1x01_P254mm_Vertical_99255f430fe9"
  AutoLinkLabel = false
  AutoPlacement = true
  LinkPlacement = pos=(86.36,-88.9,0) rot=(0,0,1;3.14159rad)
  LinkedObject = -> Shape
  Placement = pos=(86.36,-88.9,0) rot=(0,0,1;3.14159rad)
  SyncGroupVisibility = false
  TreeRank = 0
  _LinkVersion = 1
FEATURE [App::Link] J135_PinHeader_1x01_P254mm_Vertical_da6c4aed0287_ln_063  label="J49_PinHeader_1x01_P254mm_Vertical_22706fc6efa7"
  AutoLinkLabel = false
  AutoPlacement = true
  LinkPlacement = pos=(113.03,-93.98,0) rot=(0,0,1;1.5708rad)
  LinkedObject = -> Shape
  Placement = pos=(113.03,-93.98,0) rot=(0,0,1;1.5708rad)
  SyncGroupVisibility = false
  TreeRank = 0
  _LinkVersion = 1
FEATURE [App::Link] J135_PinHeader_1x01_P254mm_Vertical_da6c4aed0287_ln_064  label="J51_PinHeader_1x01_P254mm_Vertical_2f136b6726bd"
  AutoLinkLabel = false
  AutoPlacement = true
  LinkPlacement = pos=(118.11,-93.98,0) rot=(0,0,1;1.5708rad)
  LinkedObject = -> Shape
  Placement = pos=(118.11,-93.98,0) rot=(0,0,1;1.5708rad)
  SyncGroupVisibility = false
  TreeRank = 0
  _LinkVersion = 1
FEATURE [App::Link] J135_PinHeader_1x01_P254mm_Vertical_da6c4aed0287_ln_065  label="J86_PinHeader_1x01_P254mm_Vertical_1ae400d14a7d"
  AutoLinkLabel = false
  AutoPlacement = true
  LinkPlacement = pos=(105.41,-83.82,0) rot=(0,0,1;1.5708rad)
  LinkedObject = -> Shape
  Placement = pos=(105.41,-83.82,0) rot=(0,0,1;1.5708rad)
  SyncGroupVisibility = false
  TreeRank = 0
  _LinkVersion = 1
FEATURE [App::Link] J135_PinHeader_1x01_P254mm_Vertical_da6c4aed0287_ln_066  label="J93_PinHeader_1x01_P254mm_Vertical_004e2b5e8ed7"
  AutoLinkLabel = false
  AutoPlacement = true
  LinkPlacement = pos=(97.79,-81.28,0) rot=(0,0,1;1.5708rad)
  LinkedObject = -> Shape
  Placement = pos=(97.79,-81.28,0) rot=(0,0,1;1.5708rad)
  SyncGroupVisibility = false
  TreeRank = 0
  _LinkVersion = 1
FEATURE [App::Link] J135_PinHeader_1x01_P254mm_Vertical_da6c4aed0287_ln_067  label="J52_PinHeader_1x01_P254mm_Vertical_5215226168a0"
  AutoLinkLabel = false
  AutoPlacement = true
  LinkPlacement = pos=(95.25,-91.44,0) rot=(0,0,1;1.5708rad)
  LinkedObject = -> Shape
  Placement = pos=(95.25,-91.44,0) rot=(0,0,1;1.5708rad)
  SyncGroupVisibility = false
  TreeRank = 0
  _LinkVersion = 1
FEATURE [App::Link] J135_PinHeader_1x01_P254mm_Vertical_da6c4aed0287_ln_068  label="J71_PinHeader_1x01_P254mm_Vertical_6fa549b88633"
  AutoLinkLabel = false
  AutoPlacement = true
  LinkPlacement = pos=(118.11,-88.9,0) rot=(0,0,1;1.5708rad)
  LinkedObject = -> Shape
  Placement = pos=(118.11,-88.9,0) rot=(0,0,1;1.5708rad)
  SyncGroupVisibility = false
  TreeRank = 0
  _LinkVersion = 1
FEATURE [App::Link] J135_PinHeader_1x01_P254mm_Vertical_da6c4aed0287_ln_069  label="J100_PinHeader_1x01_P254mm_Vertical_9d3dc9451df2"
  AutoLinkLabel = false
  AutoPlacement = true
  LinkPlacement = pos=(115.57,-81.28,0) rot=(0,0,1;1.5708rad)
  LinkedObject = -> Shape
  Placement = pos=(115.57,-81.28,0) rot=(0,0,1;1.5708rad)
  SyncGroupVisibility = false
  TreeRank = 0
  _LinkVersion = 1
FEATURE [App::Link] J135_PinHeader_1x01_P254mm_Vertical_da6c4aed0287_ln_070  label="J26_PinHeader_1x01_P254mm_Vertical_4232218274a7"
  AutoLinkLabel = false
  AutoPlacement = true
  LinkPlacement = pos=(86.36,-68.58,0) rot=(0,0,1;3.14159rad)
  LinkedObject = -> Shape
  Placement = pos=(86.36,-68.58,0) rot=(0,0,1;3.14159rad)
  SyncGroupVisibility = false
  TreeRank = 0
  _LinkVersion = 1
FEATURE [App::Link] J135_PinHeader_1x01_P254mm_Vertical_da6c4aed0287_ln_071  label="J80_PinHeader_1x01_P254mm_Vertical_6b9a9c7a9553"
  AutoLinkLabel = false
  AutoPlacement = true
  LinkPlacement = pos=(115.57,-86.36,0) rot=(0,0,1;1.5708rad)
  LinkedObject = -> Shape
  Placement = pos=(115.57,-86.36,0) rot=(0,0,1;1.5708rad)
  SyncGroupVisibility = false
  TreeRank = 0
  _LinkVersion = 1
FEATURE [App::Link] J135_PinHeader_1x01_P254mm_Vertical_da6c4aed0287_ln_072  label="J81_PinHeader_1x01_P254mm_Vertical_3aa8ce42c7e0"
  AutoLinkLabel = false
  AutoPlacement = true
  LinkPlacement = pos=(118.11,-86.36,0) rot=(0,0,1;1.5708rad)
  LinkedObject = -> Shape
  Placement = pos=(118.11,-86.36,0) rot=(0,0,1;1.5708rad)
  SyncGroupVisibility = false
  TreeRank = 0
  _LinkVersion = 1
FEATURE [App::Link] J135_PinHeader_1x01_P254mm_Vertical_da6c4aed0287_ln_073  label="J131_PinHeader_1x01_P254mm_Vertical_eca8f13e32ef"
  AutoLinkLabel = false
  AutoPlacement = true
  LinkPlacement = pos=(118.11,-73.66,0) rot=(0,0,1;1.5708rad)
  LinkedObject = -> Shape
  Placement = pos=(118.11,-73.66,0) rot=(0,0,1;1.5708rad)
  SyncGroupVisibility = false
  TreeRank = 0
  _LinkVersion = 1
FEATURE [App::Link] J135_PinHeader_1x01_P254mm_Vertical_da6c4aed0287_ln_074  label="J112_PinHeader_1x01_P254mm_Vertical_f90d0963c6ba"
  AutoLinkLabel = false
  AutoPlacement = true
  LinkPlacement = pos=(95.25,-76.2,0) rot=(0,0,1;1.5708rad)
  LinkedObject = -> Shape
  Placement = pos=(95.25,-76.2,0) rot=(0,0,1;1.5708rad)
  SyncGroupVisibility = false
  TreeRank = 0
  _LinkVersion = 1
FEATURE [App::Link] J135_PinHeader_1x01_P254mm_Vertical_da6c4aed0287_ln_075  label="J82_PinHeader_1x01_P254mm_Vertical_53a17cb67f8b"
  AutoLinkLabel = false
  AutoPlacement = true
  LinkPlacement = pos=(95.25,-83.82,0) rot=(0,0,1;1.5708rad)
  LinkedObject = -> Shape
  Placement = pos=(95.25,-83.82,0) rot=(0,0,1;1.5708rad)
  SyncGroupVisibility = false
  TreeRank = 0
  _LinkVersion = 1
FEATURE [App::Link] J135_PinHeader_1x01_P254mm_Vertical_da6c4aed0287_ln_076  label="J111_PinHeader_1x01_P254mm_Vertical_7f8aaf0ebb89"
  AutoLinkLabel = false
  AutoPlacement = true
  LinkPlacement = pos=(118.11,-78.74,0) rot=(0,0,1;1.5708rad)
  LinkedObject = -> Shape
  Placement = pos=(118.11,-78.74,0) rot=(0,0,1;1.5708rad)
  SyncGroupVisibility = false
  TreeRank = 0
  _LinkVersion = 1
FEATURE [App::Link] J135_PinHeader_1x01_P254mm_Vertical_da6c4aed0287_ln_077  label="J84_PinHeader_1x01_P254mm_Vertical_82e8b89b00f4"
  AutoLinkLabel = false
  AutoPlacement = true
  LinkPlacement = pos=(100.33,-83.82,0) rot=(0,0,1;1.5708rad)
  LinkedObject = -> Shape
  Placement = pos=(100.33,-83.82,0) rot=(0,0,1;1.5708rad)
  SyncGroupVisibility = false
  TreeRank = 0
  _LinkVersion = 1
FEATURE [App::Link] J135_PinHeader_1x01_P254mm_Vertical_da6c4aed0287_ln_078  label="J128_PinHeader_1x01_P254mm_Vertical_dbeb0dc473ae"
  AutoLinkLabel = false
  AutoPlacement = true
  LinkPlacement = pos=(110.49,-73.66,0) rot=(0,0,1;1.5708rad)
  LinkedObject = -> Shape
  Placement = pos=(110.49,-73.66,0) rot=(0,0,1;1.5708rad)
  SyncGroupVisibility = false
  TreeRank = 0
  _LinkVersion = 1
FEATURE [App::Link] J135_PinHeader_1x01_P254mm_Vertical_da6c4aed0287_ln_079  label="J55_PinHeader_1x01_P254mm_Vertical_73db69d2a3e0"
  AutoLinkLabel = false
  AutoPlacement = true
  LinkPlacement = pos=(102.87,-91.44,0) rot=(0,0,1;1.5708rad)
  LinkedObject = -> Shape
  Placement = pos=(102.87,-91.44,0) rot=(0,0,1;1.5708rad)
  SyncGroupVisibility = false
  TreeRank = 0
  _LinkVersion = 1
FEATURE [App::Link] J135_PinHeader_1x01_P254mm_Vertical_da6c4aed0287_ln_080  label="J134_PinHeader_1x01_P254mm_Vertical_a7677ffdb21f"
  AutoLinkLabel = false
  AutoPlacement = true
  LinkPlacement = pos=(100.33,-71.12,0) rot=(0,0,1;1.5708rad)
  LinkedObject = -> Shape
  Placement = pos=(100.33,-71.12,0) rot=(0,0,1;1.5708rad)
  SyncGroupVisibility = false
  TreeRank = 0
  _LinkVersion = 1
FEATURE [App::Link] J135_PinHeader_1x01_P254mm_Vertical_da6c4aed0287_ln_081  label="J145_PinHeader_1x01_P254mm_Vertical_194bfab12c7b"
  AutoLinkLabel = false
  AutoPlacement = true
  LinkPlacement = pos=(102.87,-68.58,0) rot=(0,0,1;1.5708rad)
  LinkedObject = -> Shape
  Placement = pos=(102.87,-68.58,0) rot=(0,0,1;1.5708rad)
  SyncGroupVisibility = false
  TreeRank = 0
  _LinkVersion = 1
FEATURE [App::Link] J135_PinHeader_1x01_P254mm_Vertical_da6c4aed0287_ln_082  label="J64_PinHeader_1x01_P254mm_Vertical_025be7908b29"
  AutoLinkLabel = false
  AutoPlacement = true
  LinkPlacement = pos=(100.33,-88.9,0) rot=(0,0,1;1.5708rad)
  LinkedObject = -> Shape
  Placement = pos=(100.33,-88.9,0) rot=(0,0,1;1.5708rad)
  SyncGroupVisibility = false
  TreeRank = 0
  _LinkVersion = 1
FEATURE [App::Link] J135_PinHeader_1x01_P254mm_Vertical_da6c4aed0287_ln_083  label="J141_PinHeader_1x01_P254mm_Vertical_4ecc4c67e1f5"
  AutoLinkLabel = false
  AutoPlacement = true
  LinkPlacement = pos=(118.11,-71.12,0) rot=(0,0,1;1.5708rad)
  LinkedObject = -> Shape
  Placement = pos=(118.11,-71.12,0) rot=(0,0,1;1.5708rad)
  SyncGroupVisibility = false
  TreeRank = 0
  _LinkVersion = 1
FEATURE [App::Link] J135_PinHeader_1x01_P254mm_Vertical_da6c4aed0287_ln_084  label="J47_PinHeader_1x01_P254mm_Vertical_40d9472fa62c"
  AutoLinkLabel = false
  AutoPlacement = true
  LinkPlacement = pos=(107.95,-93.98,0) rot=(0,0,1;1.5708rad)
  LinkedObject = -> Shape
  Placement = pos=(107.95,-93.98,0) rot=(0,0,1;1.5708rad)
  SyncGroupVisibility = false
  TreeRank = 0
  _LinkVersion = 1
FEATURE [App::Link] J135_PinHeader_1x01_P254mm_Vertical_da6c4aed0287_ln_085  label="J21_PinHeader_1x01_P254mm_Vertical_694e1429e0a8"
  AutoLinkLabel = false
  AutoPlacement = true
  LinkPlacement = pos=(86.36,-81.28,0) rot=(0,0,1;3.14159rad)
  LinkedObject = -> Shape
  Placement = pos=(86.36,-81.28,0) rot=(0,0,1;3.14159rad)
  SyncGroupVisibility = false
  TreeRank = 0
  _LinkVersion = 1
FEATURE [App::Link] J135_PinHeader_1x01_P254mm_Vertical_da6c4aed0287_ln_086  label="J114_PinHeader_1x01_P254mm_Vertical_938da126562e"
  AutoLinkLabel = false
  AutoPlacement = true
  LinkPlacement = pos=(100.33,-76.2,0) rot=(0,0,1;1.5708rad)
  LinkedObject = -> Shape
  Placement = pos=(100.33,-76.2,0) rot=(0,0,1;1.5708rad)
  SyncGroupVisibility = false
  TreeRank = 0
  _LinkVersion = 1
FEATURE [App::Link] J135_PinHeader_1x01_P254mm_Vertical_da6c4aed0287_ln_087  label="J83_PinHeader_1x01_P254mm_Vertical_9f9c86e08493"
  AutoLinkLabel = false
  AutoPlacement = true
  LinkPlacement = pos=(97.79,-83.82,0) rot=(0,0,1;1.5708rad)
  LinkedObject = -> Shape
  Placement = pos=(97.79,-83.82,0) rot=(0,0,1;1.5708rad)
  SyncGroupVisibility = false
  TreeRank = 0
  _LinkVersion = 1
FEATURE [App::Link] J135_PinHeader_1x01_P254mm_Vertical_da6c4aed0287_ln_088  label="J9_PinHeader_1x01_P254mm_Vertical_8c962275048e"
  AutoLinkLabel = false
  AutoPlacement = true
  LinkPlacement = pos=(66.04,-71.12,0) rot=(0,0,1;3.14159rad)
  LinkedObject = -> Shape
  Placement = pos=(66.04,-71.12,0) rot=(0,0,1;3.14159rad)
  SyncGroupVisibility = false
  TreeRank = 0
  _LinkVersion = 1
FEATURE [App::Link] J135_PinHeader_1x01_P254mm_Vertical_da6c4aed0287_ln_089  label="J4_PinHeader_1x01_P254mm_Vertical_e79b290a1b2f"
  AutoLinkLabel = false
  AutoPlacement = true
  LinkPlacement = pos=(66.04,-83.82,0) rot=(0,0,1;3.14159rad)
  LinkedObject = -> Shape
  Placement = pos=(66.04,-83.82,0) rot=(0,0,1;3.14159rad)
  SyncGroupVisibility = false
  TreeRank = 0
  _LinkVersion = 1
FEATURE [App::Link] J135_PinHeader_1x01_P254mm_Vertical_da6c4aed0287_ln_090  label="J53_PinHeader_1x01_P254mm_Vertical_3bc9cbe78fe7"
  AutoLinkLabel = false
  AutoPlacement = true
  LinkPlacement = pos=(97.79,-91.44,0) rot=(0,0,1;1.5708rad)
  LinkedObject = -> Shape
  Placement = pos=(97.79,-91.44,0) rot=(0,0,1;1.5708rad)
  SyncGroupVisibility = false
  TreeRank = 0
  _LinkVersion = 1
FEATURE [App::Link] J135_PinHeader_1x01_P254mm_Vertical_da6c4aed0287_ln_091  label="J94_PinHeader_1x01_P254mm_Vertical_d4bf07db4549"
  AutoLinkLabel = false
  AutoPlacement = true
  LinkPlacement = pos=(100.33,-81.28,0) rot=(0,0,1;1.5708rad)
  LinkedObject = -> Shape
  Placement = pos=(100.33,-81.28,0) rot=(0,0,1;1.5708rad)
  SyncGroupVisibility = false
  TreeRank = 0
  _LinkVersion = 1
FEATURE [App::Link] J135_PinHeader_1x01_P254mm_Vertical_da6c4aed0287_ln_092  label="J56_PinHeader_1x01_P254mm_Vertical_a57a65c5627e"
  AutoLinkLabel = false
  AutoPlacement = true
  LinkPlacement = pos=(105.41,-91.44,0) rot=(0,0,1;1.5708rad)
  LinkedObject = -> Shape
  Placement = pos=(105.41,-91.44,0) rot=(0,0,1;1.5708rad)
  SyncGroupVisibility = false
  TreeRank = 0
  _LinkVersion = 1
FEATURE [App::Link] J135_PinHeader_1x01_P254mm_Vertical_da6c4aed0287_ln_093  label="J15_PinHeader_1x01_P254mm_Vertical_19fd117b2d81"
  AutoLinkLabel = false
  AutoPlacement = true
  LinkPlacement = pos=(86.36,-93.98,0) rot=(0,0,1;3.14159rad)
  LinkedObject = -> Shape
  Placement = pos=(86.36,-93.98,0) rot=(0,0,1;3.14159rad)
  SyncGroupVisibility = false
  TreeRank = 0
  _LinkVersion = 1
FEATURE [App::Link] J135_PinHeader_1x01_P254mm_Vertical_da6c4aed0287_ln_094  label="J37_PinHeader_1x01_P254mm_Vertical_0d5c741d8059"
  AutoLinkLabel = false
  AutoPlacement = true
  LinkPlacement = pos=(107.95,-96.52,0) rot=(0,0,1;1.5708rad)
  LinkedObject = -> Shape
  Placement = pos=(107.95,-96.52,0) rot=(0,0,1;1.5708rad)
  SyncGroupVisibility = false
  TreeRank = 0
  _LinkVersion = 1
FEATURE [App::Link] J135_PinHeader_1x01_P254mm_Vertical_da6c4aed0287_ln_095  label="J8_PinHeader_1x01_P254mm_Vertical_a6037da68925"
  AutoLinkLabel = false
  AutoPlacement = true
  LinkPlacement = pos=(66.04,-73.66,0) rot=(0,0,1;3.14159rad)
  LinkedObject = -> Shape
  Placement = pos=(66.04,-73.66,0) rot=(0,0,1;3.14159rad)
  SyncGroupVisibility = false
  TreeRank = 0
  _LinkVersion = 1
FEATURE [App::Link] J135_PinHeader_1x01_P254mm_Vertical_da6c4aed0287_ln_096  label="J89_PinHeader_1x01_P254mm_Vertical_7500beba03ae"
  AutoLinkLabel = false
  AutoPlacement = true
  LinkPlacement = pos=(113.03,-83.82,0) rot=(0,0,1;1.5708rad)
  LinkedObject = -> Shape
  Placement = pos=(113.03,-83.82,0) rot=(0,0,1;1.5708rad)
  SyncGroupVisibility = false
  TreeRank = 0
  _LinkVersion = 1
FEATURE [App::Link] J135_PinHeader_1x01_P254mm_Vertical_da6c4aed0287_ln_097  label="J46_PinHeader_1x01_P254mm_Vertical_9c47f70119d7"
  AutoLinkLabel = false
  AutoPlacement = true
  LinkPlacement = pos=(105.41,-93.98,0) rot=(0,0,1;1.5708rad)
  LinkedObject = -> Shape
  Placement = pos=(105.41,-93.98,0) rot=(0,0,1;1.5708rad)
  SyncGroupVisibility = false
  TreeRank = 0
  _LinkVersion = 1
FEATURE [App::Link] J135_PinHeader_1x01_P254mm_Vertical_da6c4aed0287_ln_098  label="J42_PinHeader_1x01_P254mm_Vertical_7499e4b50451"
  AutoLinkLabel = false
  AutoPlacement = true
  LinkPlacement = pos=(95.25,-93.98,0) rot=(0,0,1;1.5708rad)
  LinkedObject = -> Shape
  Placement = pos=(95.25,-93.98,0) rot=(0,0,1;1.5708rad)
  SyncGroupVisibility = false
  TreeRank = 0
  _LinkVersion = 1
FEATURE [App::Link] J135_PinHeader_1x01_P254mm_Vertical_da6c4aed0287_ln_099  label="J30_PinHeader_1x01_P254mm_Vertical_a07f460d1739"
  AutoLinkLabel = false
  AutoPlacement = true
  LinkPlacement = pos=(86.36,-96.52,0) rot=(0,0,1;3.14159rad)
  LinkedObject = -> Shape
  Placement = pos=(86.36,-96.52,0) rot=(0,0,1;3.14159rad)
  SyncGroupVisibility = false
  TreeRank = 0
  _LinkVersion = 1
FEATURE [App::Link] J135_PinHeader_1x01_P254mm_Vertical_da6c4aed0287_ln_100  label="J25_PinHeader_1x01_P254mm_Vertical_521704952a7b"
  AutoLinkLabel = false
  AutoPlacement = true
  LinkPlacement = pos=(86.36,-71.12,0) rot=(0,0,1;3.14159rad)
  LinkedObject = -> Shape
  Placement = pos=(86.36,-71.12,0) rot=(0,0,1;3.14159rad)
  SyncGroupVisibility = false
  TreeRank = 0
  _LinkVersion = 1
FEATURE [App::Link] J135_PinHeader_1x01_P254mm_Vertical_da6c4aed0287_ln_101  label="J62_PinHeader_1x01_P254mm_Vertical_7a9af1ba1e61"
  AutoLinkLabel = false
  AutoPlacement = true
  LinkPlacement = pos=(95.25,-88.9,0) rot=(0,0,1;1.5708rad)
  LinkedObject = -> Shape
  Placement = pos=(95.25,-88.9,0) rot=(0,0,1;1.5708rad)
  SyncGroupVisibility = false
  TreeRank = 0
  _LinkVersion = 1
FEATURE [App::Link] J135_PinHeader_1x01_P254mm_Vertical_da6c4aed0287_ln_102  label="J34_PinHeader_1x01_P254mm_Vertical_4abfdc338431"
  AutoLinkLabel = false
  AutoPlacement = true
  LinkPlacement = pos=(100.33,-96.52,0) rot=(0,0,1;1.5708rad)
  LinkedObject = -> Shape
  Placement = pos=(100.33,-96.52,0) rot=(0,0,1;1.5708rad)
  SyncGroupVisibility = false
  TreeRank = 0
  _LinkVersion = 1
FEATURE [App::Link] J135_PinHeader_1x01_P254mm_Vertical_da6c4aed0287_ln_103  label="J91_PinHeader_1x01_P254mm_Vertical_d819e2b56223"
  AutoLinkLabel = false
  AutoPlacement = true
  LinkPlacement = pos=(118.11,-83.82,0) rot=(0,0,1;1.5708rad)
  LinkedObject = -> Shape
  Placement = pos=(118.11,-83.82,0) rot=(0,0,1;1.5708rad)
  SyncGroupVisibility = false
  TreeRank = 0
  _LinkVersion = 1
FEATURE [App::Link] J135_PinHeader_1x01_P254mm_Vertical_da6c4aed0287_ln_104  label="J137_PinHeader_1x01_P254mm_Vertical_fb0fbb8af6ac"
  AutoLinkLabel = false
  AutoPlacement = true
  LinkPlacement = pos=(107.95,-71.12,0) rot=(0,0,1;1.5708rad)
  LinkedObject = -> Shape
  Placement = pos=(107.95,-71.12,0) rot=(0,0,1;1.5708rad)
  SyncGroupVisibility = false
  TreeRank = 0
  _LinkVersion = 1
FEATURE [App::Link] J135_PinHeader_1x01_P254mm_Vertical_da6c4aed0287_ln_105  label="J35_PinHeader_1x01_P254mm_Vertical_31a1e351a220"
  AutoLinkLabel = false
  AutoPlacement = true
  LinkPlacement = pos=(102.87,-96.52,0) rot=(0,0,1;1.5708rad)
  LinkedObject = -> Shape
  Placement = pos=(102.87,-96.52,0) rot=(0,0,1;1.5708rad)
  SyncGroupVisibility = false
  TreeRank = 0
  _LinkVersion = 1
FEATURE [App::Link] J135_PinHeader_1x01_P254mm_Vertical_da6c4aed0287_ln_106  label="J151_PinHeader_1x01_P254mm_Vertical_ebce06c72328"
  AutoLinkLabel = false
  AutoPlacement = true
  LinkPlacement = pos=(118.11,-68.58,0) rot=(0,0,1;1.5708rad)
  LinkedObject = -> Shape
  Placement = pos=(118.11,-68.58,0) rot=(0,0,1;1.5708rad)
  SyncGroupVisibility = false
  TreeRank = 0
  _LinkVersion = 1
FEATURE [App::Link] J135_PinHeader_1x01_P254mm_Vertical_da6c4aed0287_ln_107  label="J138_PinHeader_1x01_P254mm_Vertical_dc3c7c0b1a5e"
  AutoLinkLabel = false
  AutoPlacement = true
  LinkPlacement = pos=(110.49,-71.12,0) rot=(0,0,1;1.5708rad)
  LinkedObject = -> Shape
  Placement = pos=(110.49,-71.12,0) rot=(0,0,1;1.5708rad)
  SyncGroupVisibility = false
  TreeRank = 0
  _LinkVersion = 1
FEATURE [App::Link] J135_PinHeader_1x01_P254mm_Vertical_da6c4aed0287_ln_108  label="J19_PinHeader_1x01_P254mm_Vertical_f62cfaf39179"
  AutoLinkLabel = false
  AutoPlacement = true
  LinkPlacement = pos=(86.36,-86.36,0) rot=(0,0,1;3.14159rad)
  LinkedObject = -> Shape
  Placement = pos=(86.36,-86.36,0) rot=(0,0,1;3.14159rad)
  SyncGroupVisibility = false
  TreeRank = 0
  _LinkVersion = 1
FEATURE [App::Link] J135_PinHeader_1x01_P254mm_Vertical_da6c4aed0287_ln_109  label="J33_PinHeader_1x01_P254mm_Vertical_d5addac4880f"
  AutoLinkLabel = false
  AutoPlacement = true
  LinkPlacement = pos=(97.79,-96.52,0) rot=(0,0,1;1.5708rad)
  LinkedObject = -> Shape
  Placement = pos=(97.79,-96.52,0) rot=(0,0,1;1.5708rad)
  SyncGroupVisibility = false
  TreeRank = 0
  _LinkVersion = 1
FEATURE [App::Link] J135_PinHeader_1x01_P254mm_Vertical_da6c4aed0287_ln_110  label="J103_PinHeader_1x01_P254mm_Vertical_57e33908ccdf"
  AutoLinkLabel = false
  AutoPlacement = true
  LinkPlacement = pos=(97.79,-78.74,0) rot=(0,0,1;1.5708rad)
  LinkedObject = -> Shape
  Placement = pos=(97.79,-78.74,0) rot=(0,0,1;1.5708rad)
  SyncGroupVisibility = false
  TreeRank = 0
  _LinkVersion = 1
FEATURE [App::Link] J135_PinHeader_1x01_P254mm_Vertical_da6c4aed0287_ln_111  label="J43_PinHeader_1x01_P254mm_Vertical_091943085e02"
  AutoLinkLabel = false
  AutoPlacement = true
  LinkPlacement = pos=(97.79,-93.98,0) rot=(0,0,1;1.5708rad)
  LinkedObject = -> Shape
  Placement = pos=(97.79,-93.98,0) rot=(0,0,1;1.5708rad)
  SyncGroupVisibility = false
  TreeRank = 0
  _LinkVersion = 1
FEATURE [App::Link] J135_PinHeader_1x01_P254mm_Vertical_da6c4aed0287_ln_112  label="J67_PinHeader_1x01_P254mm_Vertical_fce23acc187c"
  AutoLinkLabel = false
  AutoPlacement = true
  LinkPlacement = pos=(107.95,-88.9,0) rot=(0,0,1;1.5708rad)
  LinkedObject = -> Shape
  Placement = pos=(107.95,-88.9,0) rot=(0,0,1;1.5708rad)
  SyncGroupVisibility = false
  TreeRank = 0
  _LinkVersion = 1
FEATURE [App::Link] J135_PinHeader_1x01_P254mm_Vertical_da6c4aed0287_ln_113  label="J29_PinHeader_1x01_P254mm_Vertical_e15f19f11d9b"
  AutoLinkLabel = false
  AutoPlacement = true
  LinkPlacement = pos=(86.36,-66.04,0) rot=(0,0,1;3.14159rad)
  LinkedObject = -> Shape
  Placement = pos=(86.36,-66.04,0) rot=(0,0,1;3.14159rad)
  SyncGroupVisibility = false
  TreeRank = 0
  _LinkVersion = 1
FEATURE [App::Link] J135_PinHeader_1x01_P254mm_Vertical_da6c4aed0287_ln_114  label="J22_PinHeader_1x01_P254mm_Vertical_243e8eef6838"
  AutoLinkLabel = false
  AutoPlacement = true
  LinkPlacement = pos=(86.36,-78.74,0) rot=(0,0,1;3.14159rad)
  LinkedObject = -> Shape
  Placement = pos=(86.36,-78.74,0) rot=(0,0,1;3.14159rad)
  SyncGroupVisibility = false
  TreeRank = 0
  _LinkVersion = 1
FEATURE [App::Link] J135_PinHeader_1x01_P254mm_Vertical_da6c4aed0287_ln_115  label="J40_PinHeader_1x01_P254mm_Vertical_c615dfd59d0d"
  AutoLinkLabel = false
  AutoPlacement = true
  LinkPlacement = pos=(115.57,-96.52,0) rot=(0,0,1;1.5708rad)
  LinkedObject = -> Shape
  Placement = pos=(115.57,-96.52,0) rot=(0,0,1;1.5708rad)
  SyncGroupVisibility = false
  TreeRank = 0
  _LinkVersion = 1
FEATURE [App::Link] J135_PinHeader_1x01_P254mm_Vertical_da6c4aed0287_ln_116  label="J70_PinHeader_1x01_P254mm_Vertical_23b242c6379a"
  AutoLinkLabel = false
  AutoPlacement = true
  LinkPlacement = pos=(115.57,-88.9,0) rot=(0,0,1;1.5708rad)
  LinkedObject = -> Shape
  Placement = pos=(115.57,-88.9,0) rot=(0,0,1;1.5708rad)
  SyncGroupVisibility = false
  TreeRank = 0
  _LinkVersion = 1
FEATURE [App::Link] J135_PinHeader_1x01_P254mm_Vertical_da6c4aed0287_ln_117  label="J102_PinHeader_1x01_P254mm_Vertical_f2e9ea1c82b0"
  AutoLinkLabel = false
  AutoPlacement = true
  LinkPlacement = pos=(95.25,-78.74,0) rot=(0,0,1;1.5708rad)
  LinkedObject = -> Shape
  Placement = pos=(95.25,-78.74,0) rot=(0,0,1;1.5708rad)
  SyncGroupVisibility = false
  TreeRank = 0
  _LinkVersion = 1
FEATURE [App::Link] J135_PinHeader_1x01_P254mm_Vertical_da6c4aed0287_ln_118  label="J143_PinHeader_1x01_P254mm_Vertical_43cc60315660"
  AutoLinkLabel = false
  AutoPlacement = true
  LinkPlacement = pos=(97.79,-68.58,0) rot=(0,0,1;1.5708rad)
  LinkedObject = -> Shape
  Placement = pos=(97.79,-68.58,0) rot=(0,0,1;1.5708rad)
  SyncGroupVisibility = false
  TreeRank = 0
  _LinkVersion = 1
FEATURE [App::Link] J135_PinHeader_1x01_P254mm_Vertical_da6c4aed0287_ln_119  label="J105_PinHeader_1x01_P254mm_Vertical_1208d51e8b5a"
  AutoLinkLabel = false
  AutoPlacement = true
  LinkPlacement = pos=(102.87,-78.74,0) rot=(0,0,1;1.5708rad)
  LinkedObject = -> Shape
  Placement = pos=(102.87,-78.74,0) rot=(0,0,1;1.5708rad)
  SyncGroupVisibility = false
  TreeRank = 0
  _LinkVersion = 1
FEATURE [App::Link] J135_PinHeader_1x01_P254mm_Vertical_da6c4aed0287_ln_120  label="J7_PinHeader_1x01_P254mm_Vertical_3593996b4a22"
  AutoLinkLabel = false
  AutoPlacement = true
  LinkPlacement = pos=(66.04,-76.2,0) rot=(0,0,1;3.14159rad)
  LinkedObject = -> Shape
  Placement = pos=(66.04,-76.2,0) rot=(0,0,1;3.14159rad)
  SyncGroupVisibility = false
  TreeRank = 0
  _LinkVersion = 1
FEATURE [App::Link] J135_PinHeader_1x01_P254mm_Vertical_da6c4aed0287_ln_121  label="J120_PinHeader_1x01_P254mm_Vertical_2c1d8ec06cea"
  AutoLinkLabel = false
  AutoPlacement = true
  LinkPlacement = pos=(115.57,-76.2,0) rot=(0,0,1;1.5708rad)
  LinkedObject = -> Shape
  Placement = pos=(115.57,-76.2,0) rot=(0,0,1;1.5708rad)
  SyncGroupVisibility = false
  TreeRank = 0
  _LinkVersion = 1
FEATURE [App::Link] J135_PinHeader_1x01_P254mm_Vertical_da6c4aed0287_ln_122  label="J149_PinHeader_1x01_P254mm_Vertical_a9f4566f65ae"
  AutoLinkLabel = false
  AutoPlacement = true
  LinkPlacement = pos=(113.03,-68.58,0) rot=(0,0,1;1.5708rad)
  LinkedObject = -> Shape
  Placement = pos=(113.03,-68.58,0) rot=(0,0,1;1.5708rad)
  SyncGroupVisibility = false
  TreeRank = 0
  _LinkVersion = 1
FEATURE [App::Link] J135_PinHeader_1x01_P254mm_Vertical_da6c4aed0287_ln_123  label="J38_PinHeader_1x01_P254mm_Vertical_b9e71965300f"
  AutoLinkLabel = false
  AutoPlacement = true
  LinkPlacement = pos=(110.49,-96.52,0) rot=(0,0,1;1.5708rad)
  LinkedObject = -> Shape
  Placement = pos=(110.49,-96.52,0) rot=(0,0,1;1.5708rad)
  SyncGroupVisibility = false
  TreeRank = 0
  _LinkVersion = 1
FEATURE [App::Link] J135_PinHeader_1x01_P254mm_Vertical_da6c4aed0287_ln_124  label="J121_PinHeader_1x01_P254mm_Vertical_273812b501d4"
  AutoLinkLabel = false
  AutoPlacement = true
  LinkPlacement = pos=(118.11,-76.2,0) rot=(0,0,1;1.5708rad)
  LinkedObject = -> Shape
  Placement = pos=(118.11,-76.2,0) rot=(0,0,1;1.5708rad)
  SyncGroupVisibility = false
  TreeRank = 0
  _LinkVersion = 1
FEATURE [App::Link] J135_PinHeader_1x01_P254mm_Vertical_da6c4aed0287_ln_125  label="J104_PinHeader_1x01_P254mm_Vertical_27413c652016"
  AutoLinkLabel = false
  AutoPlacement = true
  LinkPlacement = pos=(100.33,-78.74,0) rot=(0,0,1;1.5708rad)
  LinkedObject = -> Shape
  Placement = pos=(100.33,-78.74,0) rot=(0,0,1;1.5708rad)
  SyncGroupVisibility = false
  TreeRank = 0
  _LinkVersion = 1
FEATURE [App::Link] J135_PinHeader_1x01_P254mm_Vertical_da6c4aed0287_ln_126  label="J96_PinHeader_1x01_P254mm_Vertical_98c94443644b"
  AutoLinkLabel = false
  AutoPlacement = true
  LinkPlacement = pos=(105.41,-81.28,0) rot=(0,0,1;1.5708rad)
  LinkedObject = -> Shape
  Placement = pos=(105.41,-81.28,0) rot=(0,0,1;1.5708rad)
  SyncGroupVisibility = false
  TreeRank = 0
  _LinkVersion = 1
FEATURE [App::Link] J135_PinHeader_1x01_P254mm_Vertical_da6c4aed0287_ln_127  label="J54_PinHeader_1x01_P254mm_Vertical_3719b8bfbef6"
  AutoLinkLabel = false
  AutoPlacement = true
  LinkPlacement = pos=(100.33,-91.44,0) rot=(0,0,1;1.5708rad)
  LinkedObject = -> Shape
  Placement = pos=(100.33,-91.44,0) rot=(0,0,1;1.5708rad)
  SyncGroupVisibility = false
  TreeRank = 0
  _LinkVersion = 1
FEATURE [App::Link] J135_PinHeader_1x01_P254mm_Vertical_da6c4aed0287_ln_128  label="J126_PinHeader_1x01_P254mm_Vertical_8bbe0a156270"
  AutoLinkLabel = false
  AutoPlacement = true
  LinkPlacement = pos=(105.41,-73.66,0) rot=(0,0,1;1.5708rad)
  LinkedObject = -> Shape
  Placement = pos=(105.41,-73.66,0) rot=(0,0,1;1.5708rad)
  SyncGroupVisibility = false
  TreeRank = 0
  _LinkVersion = 1
FEATURE [App::Link] J135_PinHeader_1x01_P254mm_Vertical_da6c4aed0287_ln_129  label="J39_PinHeader_1x01_P254mm_Vertical_834a8c7ff8ec"
  AutoLinkLabel = false
  AutoPlacement = true
  LinkPlacement = pos=(113.03,-96.52,0) rot=(0,0,1;1.5708rad)
  LinkedObject = -> Shape
  Placement = pos=(113.03,-96.52,0) rot=(0,0,1;1.5708rad)
  SyncGroupVisibility = false
  TreeRank = 0
  _LinkVersion = 1
FEATURE [App::Link] J135_PinHeader_1x01_P254mm_Vertical_da6c4aed0287_ln_130  label="J97_PinHeader_1x01_P254mm_Vertical_19fd1eed3c14"
  AutoLinkLabel = false
  AutoPlacement = true
  LinkPlacement = pos=(107.95,-81.28,0) rot=(0,0,1;1.5708rad)
  LinkedObject = -> Shape
  Placement = pos=(107.95,-81.28,0) rot=(0,0,1;1.5708rad)
  SyncGroupVisibility = false
  TreeRank = 0
  _LinkVersion = 1
FEATURE [App::Link] J135_PinHeader_1x01_P254mm_Vertical_da6c4aed0287_ln_131  label="J48_PinHeader_1x01_P254mm_Vertical_9c303331918c"
  AutoLinkLabel = false
  AutoPlacement = true
  LinkPlacement = pos=(110.49,-93.98,0) rot=(0,0,1;1.5708rad)
  LinkedObject = -> Shape
  Placement = pos=(110.49,-93.98,0) rot=(0,0,1;1.5708rad)
  SyncGroupVisibility = false
  TreeRank = 0
  _LinkVersion = 1
FEATURE [App::Link] J135_PinHeader_1x01_P254mm_Vertical_da6c4aed0287_ln_132  label="J110_PinHeader_1x01_P254mm_Vertical_8f00b17ca227"
  AutoLinkLabel = false
  AutoPlacement = true
  LinkPlacement = pos=(115.57,-78.74,0) rot=(0,0,1;1.5708rad)
  LinkedObject = -> Shape
  Placement = pos=(115.57,-78.74,0) rot=(0,0,1;1.5708rad)
  SyncGroupVisibility = false
  TreeRank = 0
  _LinkVersion = 1
FEATURE [App::Link] J135_PinHeader_1x01_P254mm_Vertical_da6c4aed0287_ln_133  label="J150_PinHeader_1x01_P254mm_Vertical_ddb246e2b68f"
  AutoLinkLabel = false
  AutoPlacement = true
  LinkPlacement = pos=(115.57,-68.58,0) rot=(0,0,1;1.5708rad)
  LinkedObject = -> Shape
  Placement = pos=(115.57,-68.58,0) rot=(0,0,1;1.5708rad)
  SyncGroupVisibility = false
  TreeRank = 0
  _LinkVersion = 1
FEATURE [App::Link] J135_PinHeader_1x01_P254mm_Vertical_da6c4aed0287_ln_134  label="J63_PinHeader_1x01_P254mm_Vertical_6f7223393ee7"
  AutoLinkLabel = false
  AutoPlacement = true
  LinkPlacement = pos=(97.79,-88.9,0) rot=(0,0,1;1.5708rad)
  LinkedObject = -> Shape
  Placement = pos=(97.79,-88.9,0) rot=(0,0,1;1.5708rad)
  SyncGroupVisibility = false
  TreeRank = 0
  _LinkVersion = 1
FEATURE [App::Link] J135_PinHeader_1x01_P254mm_Vertical_da6c4aed0287_ln_135  label="J20_PinHeader_1x01_P254mm_Vertical_9b5adb342cd1"
  AutoLinkLabel = false
  AutoPlacement = true
  LinkPlacement = pos=(86.36,-83.82,0) rot=(0,0,1;3.14159rad)
  LinkedObject = -> Shape
  Placement = pos=(86.36,-83.82,0) rot=(0,0,1;3.14159rad)
  SyncGroupVisibility = false
  TreeRank = 0
  _LinkVersion = 1
FEATURE [App::Link] J135_PinHeader_1x01_P254mm_Vertical_da6c4aed0287_ln_136  label="J108_PinHeader_1x01_P254mm_Vertical_4000ad0be508"
  AutoLinkLabel = false
  AutoPlacement = true
  LinkPlacement = pos=(110.49,-78.74,0) rot=(0,0,1;1.5708rad)
  LinkedObject = -> Shape
  Placement = pos=(110.49,-78.74,0) rot=(0,0,1;1.5708rad)
  SyncGroupVisibility = false
  TreeRank = 0
  _LinkVersion = 1
FEATURE [App::Link] J135_PinHeader_1x01_P254mm_Vertical_da6c4aed0287_ln_137  label="J101_PinHeader_1x01_P254mm_Vertical_7f03a88063f0"
  AutoLinkLabel = false
  AutoPlacement = true
  LinkPlacement = pos=(118.11,-81.28,0) rot=(0,0,1;1.5708rad)
  LinkedObject = -> Shape
  Placement = pos=(118.11,-81.28,0) rot=(0,0,1;1.5708rad)
  SyncGroupVisibility = false
  TreeRank = 0
  _LinkVersion = 1
FEATURE [App::Link] J135_PinHeader_1x01_P254mm_Vertical_da6c4aed0287_ln_138  label="J75_PinHeader_1x01_P254mm_Vertical_5c27870e4a0a"
  AutoLinkLabel = false
  AutoPlacement = true
  LinkPlacement = pos=(102.87,-86.36,0) rot=(0,0,1;1.5708rad)
  LinkedObject = -> Shape
  Placement = pos=(102.87,-86.36,0) rot=(0,0,1;1.5708rad)
  SyncGroupVisibility = false
  TreeRank = 0
  _LinkVersion = 1
FEATURE [App::Link] J135_PinHeader_1x01_P254mm_Vertical_da6c4aed0287_ln_139  label="J23_PinHeader_1x01_P254mm_Vertical_aefb021bfb32"
  AutoLinkLabel = false
  AutoPlacement = true
  LinkPlacement = pos=(86.36,-76.2,0) rot=(0,0,1;3.14159rad)
  LinkedObject = -> Shape
  Placement = pos=(86.36,-76.2,0) rot=(0,0,1;3.14159rad)
  SyncGroupVisibility = false
  TreeRank = 0
  _LinkVersion = 1
FEATURE [App::Link] J135_PinHeader_1x01_P254mm_Vertical_da6c4aed0287_ln_140  label="J6_PinHeader_1x01_P254mm_Vertical_5fa077225f2d"
  AutoLinkLabel = false
  AutoPlacement = true
  LinkPlacement = pos=(66.04,-78.74,0) rot=(0,0,1;3.14159rad)
  LinkedObject = -> Shape
  Placement = pos=(66.04,-78.74,0) rot=(0,0,1;3.14159rad)
  SyncGroupVisibility = false
  TreeRank = 0
  _LinkVersion = 1
FEATURE [App::Link] J135_PinHeader_1x01_P254mm_Vertical_da6c4aed0287_ln_141  label="J65_PinHeader_1x01_P254mm_Vertical_97dac205dec5"
  AutoLinkLabel = false
  AutoPlacement = true
  LinkPlacement = pos=(102.87,-88.9,0) rot=(0,0,1;1.5708rad)
  LinkedObject = -> Shape
  Placement = pos=(102.87,-88.9,0) rot=(0,0,1;1.5708rad)
  SyncGroupVisibility = false
  TreeRank = 0
  _LinkVersion = 1
FEATURE [App::Link] J135_PinHeader_1x01_P254mm_Vertical_da6c4aed0287_ln_142  label="J132_PinHeader_1x01_P254mm_Vertical_bcae4cc085b8"
  AutoLinkLabel = false
  AutoPlacement = true
  LinkPlacement = pos=(95.25,-71.12,0) rot=(0,0,1;1.5708rad)
  LinkedObject = -> Shape
  Placement = pos=(95.25,-71.12,0) rot=(0,0,1;1.5708rad)
  SyncGroupVisibility = false
  TreeRank = 0
  _LinkVersion = 1
FEATURE [App::Link] J135_PinHeader_1x01_P254mm_Vertical_da6c4aed0287_ln_143  label="J76_PinHeader_1x01_P254mm_Vertical_365826054727"
  AutoLinkLabel = false
  AutoPlacement = true
  LinkPlacement = pos=(105.41,-86.36,0) rot=(0,0,1;1.5708rad)
  LinkedObject = -> Shape
  Placement = pos=(105.41,-86.36,0) rot=(0,0,1;1.5708rad)
  SyncGroupVisibility = false
  TreeRank = 0
  _LinkVersion = 1
FEATURE [App::Link] J135_PinHeader_1x01_P254mm_Vertical_da6c4aed0287_ln_144  label="J11_PinHeader_1x01_P254mm_Vertical_3d1c2f6a0c8f"
  AutoLinkLabel = false
  AutoPlacement = true
  LinkPlacement = pos=(66.04,-66.04,0) rot=(0,0,1;3.14159rad)
  LinkedObject = -> Shape
  Placement = pos=(66.04,-66.04,0) rot=(0,0,1;3.14159rad)
  SyncGroupVisibility = false
  TreeRank = 0
  _LinkVersion = 1
FEATURE [App::Link] J135_PinHeader_1x01_P254mm_Vertical_da6c4aed0287_ln_145  label="J79_PinHeader_1x01_P254mm_Vertical_63aea639777b"
  AutoLinkLabel = false
  AutoPlacement = true
  LinkPlacement = pos=(113.03,-86.36,0) rot=(0,0,1;1.5708rad)
  LinkedObject = -> Shape
  Placement = pos=(113.03,-86.36,0) rot=(0,0,1;1.5708rad)
  SyncGroupVisibility = false
  TreeRank = 0
  _LinkVersion = 1
FEATURE [App::Link] J135_PinHeader_1x01_P254mm_Vertical_da6c4aed0287_ln_146  label="J115_PinHeader_1x01_P254mm_Vertical_39be94face5b"
  AutoLinkLabel = false
  AutoPlacement = true
  LinkPlacement = pos=(102.87,-76.2,0) rot=(0,0,1;1.5708rad)
  LinkedObject = -> Shape
  Placement = pos=(102.87,-76.2,0) rot=(0,0,1;1.5708rad)
  SyncGroupVisibility = false
  TreeRank = 0
  _LinkVersion = 1
FEATURE [App::Link] J135_PinHeader_1x01_P254mm_Vertical_da6c4aed0287_ln_147  label="J72_PinHeader_1x01_P254mm_Vertical_fd6252600da0"
  AutoLinkLabel = false
  AutoPlacement = true
  LinkPlacement = pos=(95.25,-86.36,0) rot=(0,0,1;1.5708rad)
  LinkedObject = -> Shape
  Placement = pos=(95.25,-86.36,0) rot=(0,0,1;1.5708rad)
  SyncGroupVisibility = false
  TreeRank = 0
  _LinkVersion = 1
FEATURE [App::Link] J135_PinHeader_1x01_P254mm_Vertical_da6c4aed0287_ln_148  label="J32_PinHeader_1x01_P254mm_Vertical_75ac60a93074"
  AutoLinkLabel = false
  AutoPlacement = true
  LinkPlacement = pos=(95.25,-96.52,0) rot=(0,0,1;1.5708rad)
  LinkedObject = -> Shape
  Placement = pos=(95.25,-96.52,0) rot=(0,0,1;1.5708rad)
  SyncGroupVisibility = false
  TreeRank = 0
  _LinkVersion = 1
FEATURE [App::Part] Top_97b0
  ClaimAllChildren = false
  ExportMode = 1
  Group = -> [Shape,J135_PinHeader_1x01_P254mm_Vertical_da6c4aed0287_ln_,J135_PinHeader_1x01_P254mm_Vertical_da6c4aed0287_ln_001,J135_PinHeader_1x01_P254mm_Vertical_da6c4aed0287_ln_002,J135_PinHeader_1x01_P254mm_Vertical_da6c4aed0287_ln_003,J135_PinHeader_1x01_P254mm_Vertical_da6c4aed0287_ln_004,J135_PinHeader_1x01_P254mm_Vertical_da6c4aed0287_ln_005,J135_PinHeader_1x01_P254mm_Vertical_da6c4aed0287_ln_006,+144 more]
  Origin = -> Origin003
  TreeRank = 0
  _ExportChildren = -> [Shape,J135_PinHeader_1x01_P254mm_Vertical_da6c4aed0287_ln_,J135_PinHeader_1x01_P254mm_Vertical_da6c4aed0287_ln_001,J135_PinHeader_1x01_P254mm_Vertical_da6c4aed0287_ln_002,J135_PinHeader_1x01_P254mm_Vertical_da6c4aed0287_ln_003,J135_PinHeader_1x01_P254mm_Vertical_da6c4aed0287_ln_004,J135_PinHeader_1x01_P254mm_Vertical_da6c4aed0287_ln_005,J135_PinHeader_1x01_P254mm_Vertical_da6c4aed0287_ln_006,+144 more]
  _GroupVersion = 1
FEATURE [Part::Feature] Shape001  label="BT1_PinHeader_1x02_P254mm_Vertical_64228b7c207f"
  Placement = pos=(124.46,-92.71,-1.6) rot=(0,1,0;3.14159rad)
  TreeRank = 0
  shape: bbox 2.54 x 5.08 x 11.54 mm, 52 faces (baked)
FEATURE [Part::Feature] Part__Feature022  label="pp3_battery"
  TreeRank = 0
  shape: bbox 1.5 x 6.35 x 6.35 mm, 3 faces, 0 solids (baked)
FEATURE [Part::Feature] Part__Feature023  label="pp3_battery001"
  TreeRank = 0
  shape: bbox 42.82 x 26 x 16.6 mm, 196 faces, 0 solids (baked)
FEATURE [Part::Feature] Part__Feature024  label="pp3_battery002"
  TreeRank = 0
  shape: bbox 3.2 x 8 x 8 mm, 11 faces, 0 solids (baked)
FEATURE [Part::Feature] Part__Feature025  label="pp3_battery003"
  TreeRank = 0
  shape: bbox 0.0001965 x 6.345 x 2.963e-07 mm, 1 faces, 0 solids (baked)
FEATURE [Part::Feature] Part__Feature026  label="pp3_battery004"
  TreeRank = 0
  shape: bbox 0.8457 x 25.33 x 15.74 mm, 1 faces, 0 solids (baked)
FEATURE [Part::Feature] Part__Feature027  label="pp3_battery005"
  TreeRank = 0
  shape: bbox 0.0001967 x 6.334 x 2.965e-07 mm, 1 faces, 0 solids (baked)
FEATURE [Part::Feature] Part__Feature028  label="pp3_battery006"
  TreeRank = 0
  shape: bbox 0.0001965 x 6.345 x 2.963e-07 mm, 1 faces, 0 solids (baked)
FEATURE [Part::Feature] Part__Feature029  label="pp3_battery007"
  TreeRank = 0
  shape: bbox 0.0001967 x 6.334 x 2.965e-07 mm, 1 faces, 0 solids (baked)
FEATURE [Part::Feature] Part__Feature030  label="pp3_battery008"
  TreeRank = 0
  shape: bbox 3 x 8.776 x 7.6 mm, 28 faces, 0 solids (baked)
FEATURE [App::Part] pp3_battery  label="BT1_pp3_battery009_64228b7c207f[2]"
  ClaimAllChildren = false
  ExportMode = 1
  Group = -> [Part__Feature022,Part__Feature023,Part__Feature024,Part__Feature025,Part__Feature026,Part__Feature027,Part__Feature028,Part__Feature029,Part__Feature030]
  Origin = -> Origin009
  Placement = pos=(108.99,-80.68,0.67) rot=(0.707107,-0.707107,0;3.14159rad)
  TreeRank = 0
  _ExportChildren = -> [Part__Feature022,Part__Feature023,Part__Feature024,Part__Feature025,Part__Feature026,Part__Feature027,Part__Feature028,Part__Feature029,Part__Feature030]
  _GroupVersion = 1
FEATURE [Part::Feature] Part__Feature031  label="arduino_nano_socket"
  TreeRank = 0
  shape: bbox 2.54 x 38.1 x 10.1 mm, 475 faces (baked)
FEATURE [Part::Feature] Part__Feature032  label="arduino_nano_socket001"
  TreeRank = 0
  shape: bbox 2.54 x 38.1 x 10.1 mm, 475 faces (baked)
FEATURE [Part::Feature] Part__Feature033  label="arduino_nano_socket002"
  TreeRank = 0
  shape: bbox 18 x 43.2 x 4.77 mm, 378 faces (baked)
FEATURE [Part::Feature] Part__Feature034  label="arduino_nano_socket003"
  TreeRank = 0
  shape: bbox 2.54 x 5 x 11.75 mm, 46 faces (baked)
FEATURE [Part::Feature] Part__Feature035  label="arduino_nano_socket004"
  TreeRank = 0
  shape: bbox 2.54 x 5 x 11.75 mm, 46 faces (baked)
FEATURE [Part::Feature] Part__Feature036  label="arduino_nano_socket005"
  TreeRank = 0
  shape: bbox 2.54 x 5 x 11.75 mm, 46 faces (baked)
FEATURE [Part::Feature] Part__Feature037  label="arduino_nano_socket006"
  TreeRank = 0
  shape: bbox 2.54 x 38.1 x 11.75 mm, 364 faces (baked)
FEATURE [Part::Feature] Part__Feature038  label="arduino_nano_socket007"
  TreeRank = 0
  shape: bbox 2.54 x 38.1 x 11.75 mm, 364 faces (baked)
FEATURE [Part::Feature] Part__Feature039  label="arduino_nano_socket008"
  TreeRank = 0
  shape: bbox 11.25 x 11.25 x 1.2 mm, 1867 faces (baked)
FEATURE [Part::Feature] Part__Feature040  label="arduino_nano_socket009"
  TreeRank = 0
  shape: bbox 9.287 x 10.2 x 1.9 mm, 717 faces (baked)
FEATURE [Part::Feature] Part__Feature041  label="arduino_nano_socket010"
  TreeRank = 0
  shape: bbox 1.813 x 3.8 x 0.6 mm, 74 faces (baked)
FEATURE [Part::Feature] Part__Feature042  label="arduino_nano_socket011"
  TreeRank = 0
  shape: bbox 1.813 x 3.8 x 0.6 mm, 74 faces (baked)
FEATURE [Part::Feature] Part__Feature043  label="arduino_nano_socket012"
  TreeRank = 0
  shape: bbox 1.813 x 3.8 x 0.6 mm, 74 faces (baked)
FEATURE [Part::Feature] Part__Feature044  label="arduino_nano_socket013"
  TreeRank = 0
  shape: bbox 1.813 x 3.8 x 0.6 mm, 74 faces (baked)
FEATURE [Part::Feature] Part__Feature045  label="arduino_nano_socket014"
  TreeRank = 0
  shape: bbox 1.813 x 3.8 x 0.6 mm, 74 faces (baked)
FEATURE [Part::Feature] Part__Feature046  label="arduino_nano_socket015"
  TreeRank = 0
  shape: bbox 2.138 x 4.438 x 0.5452 mm, 51 faces (baked)
FEATURE [Part::Feature] Part__Feature047  label="arduino_nano_socket016"
  TreeRank = 0
  shape: bbox 1.2 x 1.4 x 0.5 mm, 6 faces (baked)
FEATURE [Part::Feature] Part__Feature048  label="arduino_nano_socket017"
  TreeRank = 0
  shape: bbox 2.138 x 4.438 x 0.5452 mm, 51 faces (baked)
FEATURE [Part::Feature] Part__Feature049  label="arduino_nano_socket018"
  TreeRank = 0
  shape: bbox 1.2 x 1.4 x 0.5 mm, 6 faces (baked)
FEATURE [Part::Feature] Part__Feature050  label="arduino_nano_socket019"
  TreeRank = 0
  shape: bbox 2.138 x 4.438 x 0.5452 mm, 51 faces (baked)
FEATURE [Part::Feature] Part__Feature051  label="arduino_nano_socket020"
  TreeRank = 0
  shape: bbox 1.2 x 1.4 x 0.5 mm, 6 faces (baked)
FEATURE [Part::Feature] Part__Feature052  label="arduino_nano_socket021"
  TreeRank = 0
  shape: bbox 2.138 x 4.438 x 0.5452 mm, 51 faces (baked)
FEATURE [Part::Feature] Part__Feature053  label="arduino_nano_socket022"
  TreeRank = 0
  shape: bbox 1.2 x 1.4 x 0.5 mm, 6 faces (baked)
FEATURE [Part::Feature] Part__Feature054  label="arduino_nano_socket023"
  TreeRank = 0
  shape: bbox 3.394 x 3.394 x 0.8 mm, 71 faces (baked)
FEATURE [Part::Feature] Part__Feature055  label="arduino_nano_socket024"
  TreeRank = 0
  shape: bbox 11.03 x 9.475 x 3.822 mm, 243 faces (baked)
FEATURE [Part::Feature] Part__Feature056  label="arduino_nano_socket025"
  TreeRank = 0
  shape: bbox 7.7 x 8.2 x 4.5 mm, 127 faces (baked)
FEATURE [Part::Feature] Part__Feature057  label="arduino_nano_socket026"
  TreeRank = 0
  shape: bbox 0.5011 x 9.423 x 2.551 mm, 31 faces (baked)
FEATURE [Part::Feature] Part__Feature058  label="arduino_nano_socket027"
  TreeRank = 0
  shape: bbox 0.5011 x 9.423 x 2.551 mm, 31 faces (baked)
FEATURE [Part::Feature] Part__Feature059  label="arduino_nano_socket028"
  TreeRank = 0
  shape: bbox 0.5011 x 9.423 x 2.551 mm, 31 faces (baked)
FEATURE [Part::Feature] Part__Feature060  label="arduino_nano_socket029"
  TreeRank = 0
  shape: bbox 0.5011 x 9.423 x 2.551 mm, 31 faces (baked)
FEATURE [Part::Feature] Part__Feature061  label="arduino_nano_socket030"
  TreeRank = 0
  shape: bbox 0.5011 x 9.423 x 2.551 mm, 31 faces (baked)
FEATURE [Part::Feature] Part__Feature062  label="arduino_nano_socket031"
  TreeRank = 0
  shape: bbox 1.701 x 4.001 x 1.811 mm, 124 faces (baked)
FEATURE [Part::Feature] Part__Feature063  label="arduino_nano_socket032"
  TreeRank = 0
  shape: bbox 1.701 x 4.001 x 1.811 mm, 124 faces (baked)
FEATURE [Part::Feature] Part__Feature064  label="arduino_nano_socket033"
  TreeRank = 0
  shape: bbox 5.2 x 2.8 x 2.15 mm, 77 faces (baked)
FEATURE [Part::Feature] Part__Feature065  label="arduino_nano_socket034"
  TreeRank = 0
  shape: bbox 4 x 3 x 1.65 mm, 72 faces (baked)
FEATURE [Part::Feature] Part__Feature066  label="arduino_nano_socket035"
  TreeRank = 0
  shape: bbox 6.5 x 8.3 x 1.689 mm, 194 faces (baked)
FEATURE [Part::Feature] Part__Feature067  label="arduino_nano_socket036"
  TreeRank = 0
  shape: bbox 4.916 x 1.7 x 1.384 mm, 85 faces (baked)
FEATURE [Part::Feature] Part__Feature068  label="arduino_nano_socket037"
  TreeRank = 0
  shape: bbox 3.2 x 1.3 x 0.3 mm, 18 faces (baked)
FEATURE [Part::Feature] Part__Feature069  label="arduino_nano_socket038"
  TreeRank = 0
  shape: bbox 3.2 x 1.5 x 0.455 mm, 147 faces (baked)
FEATURE [Part::Feature] Part__Feature070  label="arduino_nano_socket039"
  TreeRank = 0
  shape: bbox 0.4001 x 0.9095 x 0.4736 mm, 15 faces (baked)
FEATURE [Part::Feature] Part__Feature071  label="arduino_nano_socket040"
  TreeRank = 0
  shape: bbox 0.4001 x 0.9095 x 0.4736 mm, 15 faces (baked)
FEATURE [Part::Feature] Part__Feature072  label="arduino_nano_socket041"
  TreeRank = 0
  shape: bbox 0.4001 x 0.9095 x 0.4736 mm, 15 faces (baked)
FEATURE [Part::Feature] Part__Feature073  label="arduino_nano_socket042"
  TreeRank = 0
  shape: bbox 0.4001 x 0.9095 x 0.4736 mm, 15 faces (baked)
FEATURE [Part::Feature] Part__Feature074  label="arduino_nano_socket043"
  TreeRank = 0
  shape: bbox 0.4001 x 0.9095 x 0.4736 mm, 15 faces (baked)
FEATURE [Part::Feature] Part__Feature075  label="arduino_nano_socket044"
  TreeRank = 0
  shape: bbox 0.4001 x 0.9095 x 0.4736 mm, 15 faces (baked)
FEATURE [Part::Feature] Part__Feature076  label="arduino_nano_socket045"
  TreeRank = 0
  shape: bbox 0.4001 x 0.9095 x 0.4736 mm, 15 faces (baked)
FEATURE [Part::Feature] Part__Feature077  label="arduino_nano_socket046"
  TreeRank = 0
  shape: bbox 0.4001 x 0.9095 x 0.4736 mm, 15 faces (baked)
FEATURE [Part::Feature] Part__Feature078  label="arduino_nano_socket047"
  TreeRank = 0
  shape: bbox 3.2 x 1.3 x 0.3 mm, 18 faces (baked)
FEATURE [Part::Feature] Part__Feature079  label="arduino_nano_socket048"
  TreeRank = 0
  shape: bbox 3.2 x 1.5 x 0.455 mm, 136 faces (baked)
FEATURE [Part::Feature] Part__Feature080  label="arduino_nano_socket049"
  TreeRank = 0
  shape: bbox 0.4001 x 0.9095 x 0.4736 mm, 15 faces (baked)
FEATURE [Part::Feature] Part__Feature081  label="arduino_nano_socket050"
  TreeRank = 0
  shape: bbox 0.4001 x 0.9095 x 0.4736 mm, 15 faces (baked)
FEATURE [Part::Feature] Part__Feature082  label="arduino_nano_socket051"
  TreeRank = 0
  shape: bbox 0.4001 x 0.9095 x 0.4736 mm, 15 faces (baked)
FEATURE [Part::Feature] Part__Feature083  label="arduino_nano_socket052"
  TreeRank = 0
  shape: bbox 0.4001 x 0.9095 x 0.4736 mm, 15 faces (baked)
FEATURE [Part::Feature] Part__Feature084  label="arduino_nano_socket053"
  TreeRank = 0
  shape: bbox 0.4001 x 0.9095 x 0.4736 mm, 15 faces (baked)
FEATURE [Part::Feature] Part__Feature085  label="arduino_nano_socket054"
  TreeRank = 0
  shape: bbox 0.4001 x 0.9095 x 0.4736 mm, 15 faces (baked)
FEATURE [Part::Feature] Part__Feature086  label="arduino_nano_socket055"
  TreeRank = 0
  shape: bbox 0.4001 x 0.9095 x 0.4736 mm, 15 faces (baked)
FEATURE [Part::Feature] Part__Feature087  label="arduino_nano_socket056"
  TreeRank = 0
  shape: bbox 0.4001 x 0.9095 x 0.4736 mm, 15 faces (baked)
FEATURE [App::Part] arduino_nano_socket  label="XA1_arduino_nano_socket057_d5ff97aaa247"
  ClaimAllChildren = false
  ExportMode = 1
  Group = -> [Part__Feature031,Part__Feature032,Part__Feature033,Part__Feature034,Part__Feature035,Part__Feature036,Part__Feature037,Part__Feature038,Part__Feature039,Part__Feature040,Part__Feature041,Part__Feature042,Part__Feature043,Part__Feature044,Part__Feature045,Part__Feature046,Part__Feature047,Part__Feature048,Part__Feature049,Part__Feature050,Part__Feature051,Part__Feature052,Part__Feature053,+34 more]
  Origin = -> Origin010
  Placement = pos=(76.2,-101.6,-1.6) rot=(1,0,0;3.14159rad)
  TreeRank = 0
  _ExportChildren = -> [Part__Feature031,Part__Feature032,Part__Feature033,Part__Feature034,Part__Feature035,Part__Feature036,Part__Feature037,Part__Feature038,Part__Feature039,Part__Feature040,Part__Feature041,Part__Feature042,Part__Feature043,Part__Feature044,Part__Feature045,Part__Feature046,Part__Feature047,Part__Feature048,Part__Feature049,Part__Feature050,Part__Feature051,Part__Feature052,Part__Feature053,+34 more]
  _GroupVersion = 1
FEATURE [Part::Feature] Shape002  label="SW1_1_219a87e7a09f"
  Placement = pos=(124.46,-69.12,-1.6) rot=(0.707107,-0.707107,0;3.14159rad)
  TreeRank = 0
  shape: bbox 8.4 x 8.6 x 7.6 mm, 200 faces (baked)
FEATURE [Part::Feature] Shape003  label="D1_D_DO-41_SOD81_P10.16mm_Horizontal_32ec51f60e8f"
  Placement = pos=(124.46,-78.74,-1.6) rot=(0.707107,-0.707107,0;3.14159rad)
  TreeRank = 0
  shape: bbox 2.72 x 11.16 x 5.71 mm, 15 faces (baked)
FEATURE [App::Part] Bot_97b0
  ClaimAllChildren = false
  ExportMode = 1
  Group = -> [Shape001,pp3_battery,arduino_nano_socket,Shape002,Shape003]
  Origin = -> Origin004
  TreeRank = 0
  _ExportChildren = -> [Shape001,pp3_battery,arduino_nano_socket,Shape002,Shape003]
  _GroupVersion = 1
FEATURE [App::Part] Step_Models_97b0
  ClaimAllChildren = false
  ExportMode = 1
  Group = -> [Top_97b0,Bot_97b0]
  Origin = -> Origin002
  TreeRank = 0
  _ExportChildren = -> [Top_97b0,Bot_97b0]
  _GroupVersion = 1
FEATURE [Part::Feature] pads_area156001  label="topPads_97b0"
  Placement = pos=(0,0,0.02) rot=(0,0,1;0rad)
  TreeRank = 0
  shape: bbox 61.02 x 47.54 x 2e-07 mm, 217 faces, 0 solids (baked)
FEATURE [Part::Feature] Shape004001  label="topTracks_97b0"
  Placement = pos=(0,0,0.01) rot=(0,0,1;0rad)
  TreeRank = 0
  shape: bbox 58.24 x 47.24 x 2e-07 mm, 57 faces, 0 solids (baked)
FEATURE [Part::Feature] pads_area156158001  label="botPads_97b0"
  Placement = pos=(0,0,-1.62) rot=(0,0,1;0rad)
  TreeRank = 0
  shape: bbox 61.02 x 47.54 x 2e-07 mm, 217 faces, 0 solids (baked)
FEATURE [Part::Feature] Shape004002001  label="botTracks_97b0"
  Placement = pos=(0,0,-1.61) rot=(0,0,1;0rad)
  TreeRank = 0
  shape: bbox 55.01 x 48.01 x 2e-07 mm, 22 faces, 0 solids (baked)
FEATURE [Part::Feature] zones_area001  label="botZones_97b0"
  Placement = pos=(0,0,-1.61) rot=(0,0,1;0rad)
  TreeRank = 0
  shape: bbox 76.25 x 50.85 x 2e-07 mm, 12 faces, 0 solids (baked)
FEATURE [Part::Feature] topSilks_63d7
  Placement = pos=(0.75,-0.7,0.07) rot=(0,0,1;0rad)
  TreeRank = 0
  shape: bbox 65.42 x 43.86 x 2e-07 mm, 209 faces, 0 solids (baked)
FEATURE [Part::Feature] botSilks_6e03
  Placement = pos=(0.8,-0.8,-1.67) rot=(0,0,1;0rad)
  TreeRank = 0
  shape: bbox 60.43 x 46.01 x 2e-07 mm, 46 faces, 0 solids (baked)
FEATURE [App::Part] Board_Geoms_97b0
  ClaimAllChildren = false
  ExportMode = 1
  Group = -> [Pcb_97b0,PCB_Sketch_97b0,pads_area156001,Shape004001,pads_area156158001,Shape004002001,zones_area001,topSilks_63d7,botSilks_6e03]
  Origin = -> Origin
  TreeRank = 0
  _ExportChildren = -> [Pcb_97b0,PCB_Sketch_97b0,pads_area156001,Shape004001,pads_area156158001,Shape004002001,zones_area001,topSilks_63d7,botSilks_6e03]
  _GroupVersion = 1
FEATURE [App::Part] Board_97b0  label="8x8_badge"
  ClaimAllChildren = false
  ExportMode = 1
  Group = -> [Local_CS_97b0,Board_Geoms_97b0,Step_Models_97b0]
  Origin = -> Origin001
  TreeRank = 0
  _ExportChildren = -> [Local_CS_97b0,Board_Geoms_97b0,Step_Models_97b0]
  _GroupVersion = 1
